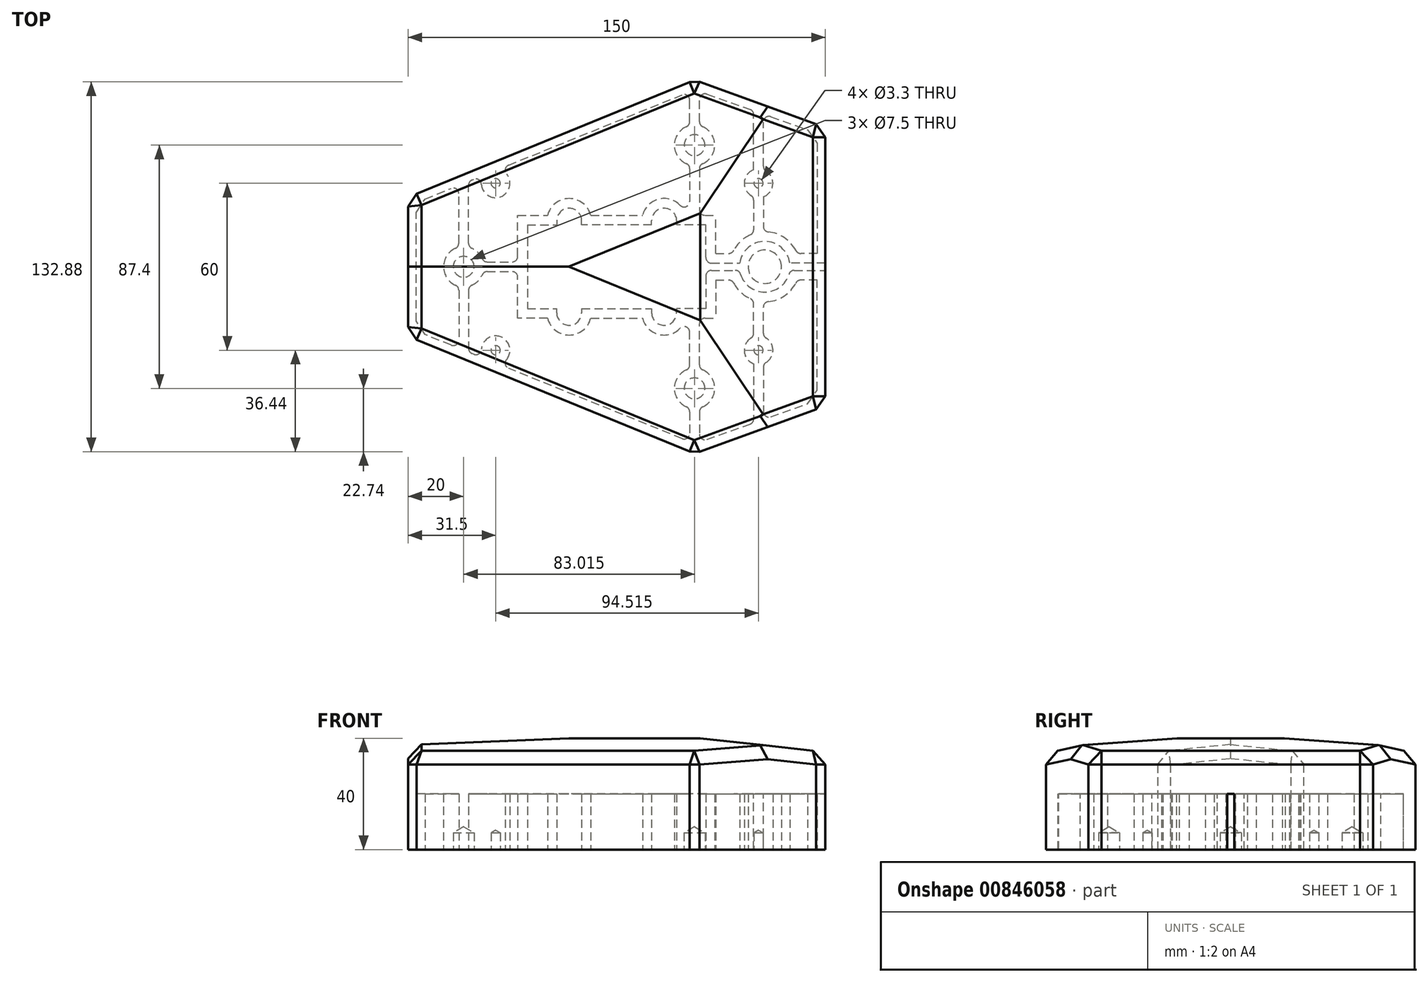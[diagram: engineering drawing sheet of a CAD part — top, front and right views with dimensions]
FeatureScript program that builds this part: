
annotation { "Feature Type Name" : "Feature", "Feature Type Description" : "" }
export const myFeature = defineFeature(function(context is Context, id is Id, definition is map)
    precondition{}
    {
        {
            var Q0;
            Q0=qCreatedBy(makeId("Top.planeOp"),FACE);
            var sketch = newSketch(context, id + "F0", { "sketchPlane" : qUnion([Q0])});
            skLineSegment(sketch, "E0", {"start": v(0, 0) * mm, "end": v(0, -50) * mm});
            skLineSegment(sketch, "E1", {"start": v(0, 0) * mm, "end": v(0, 50) * mm});
            skLineSegment(sketch, "E2", {"start": v(0, 50) * mm, "end": v(-46.98, 67.1) * mm});
            skLineSegment(sketch, "E3", {"start": v(-150, 0) * mm, "end": v(-150, 25) * mm});
            skLineSegment(sketch, "E4", {"start": v(-150, 0) * mm, "end": v(-150, -25) * mm});
            skLineSegment(sketch, "E5", {"start": v(-150, 25) * mm, "end": v(-46.98, 67.1) * mm});
            skLineSegment(sketch, "E6", {"start": v(-150, 0) * mm, "end": v(0, 0) * mm});
            skLineSegment(sketch, "E7.MirrorCS", {"start": v(0, -50) * mm, "end": v(-46.98, -67.1) * mm});
            skLineSegment(sketch, "E8", {"start": v(-150, -25) * mm, "end": v(-46.98, -67.1) * mm});
            skLineSegment(sketch, "E9.bottom", {"start": v(-106.68, 14.6) * mm, "end": v(-96.18, 14.6) * mm});
            skLineSegment(sketch, "E9.top", {"start": v(-106.68, -14.6) * mm, "end": v(-96.18, -14.6) * mm});
            skLineSegment(sketch, "E9.right", {"start": v(-43.33, 14.6) * mm, "end": v(-43.33, -14.6) * mm});
            skLineSegment(sketch, "E10", {"start": v(-96.18, 14.6) * mm, "end": v(-96.18, 16.53) * mm});
            skLineSegment(sketch, "E11", {"start": v(-87.98, 14.6) * mm, "end": v(-87.98, 16.53) * mm});
            skArc(sketch, "E12", {"start": v(-87.98, 16.53) * mm, "mid": v(-92.08, 20.63) * mm, "end": v(-96.18, 16.53) * mm});
            skLineSegment(sketch, "E13.trimOffspring", {"start": v(-87.98, 14.6) * mm, "end": v(-62.02, 14.6) * mm});
            skArc(sketch, "E14.MirrorCS", {"start": v(-62.02, 16.53) * mm, "mid": v(-57.92, 20.63) * mm, "end": v(-53.82, 16.53) * mm});
            skLineSegment(sketch, "E15.MirrorCS", {"start": v(-53.82, 14.6) * mm, "end": v(-53.82, 16.53) * mm});
            skLineSegment(sketch, "E16.MirrorCS", {"start": v(-62.02, 14.6) * mm, "end": v(-62.02, 16.53) * mm});
            skLineSegment(sketch, "E17.MirrorCS", {"start": v(-96.18, -14.6) * mm, "end": v(-96.18, -16.53) * mm});
            skArc(sketch, "E18.MirrorCS", {"start": v(-87.98, -16.53) * mm, "mid": v(-92.08, -20.63) * mm, "end": v(-96.18, -16.53) * mm});
            skLineSegment(sketch, "E19.MirrorCS", {"start": v(-87.98, -14.6) * mm, "end": v(-87.98, -16.53) * mm});
            skLineSegment(sketch, "E20.MirrorCS", {"start": v(-62.03, -14.6) * mm, "end": v(-62.02, -16.53) * mm});
            skArc(sketch, "E21.MirrorCS", {"start": v(-62.02, -16.53) * mm, "mid": v(-57.92, -20.63) * mm, "end": v(-53.83, -16.53) * mm});
            skLineSegment(sketch, "E22.MirrorCS", {"start": v(-53.83, -14.6) * mm, "end": v(-53.83, -16.53) * mm});
            skLineSegment(sketch, "E23.trimOffspring", {"start": v(-87.98, -14.6) * mm, "end": v(-62.03, -14.6) * mm});
            skLineSegment(sketch, "E24.trimOffspring", {"start": v(-53.83, -14.6) * mm, "end": v(-43.33, -14.6) * mm});
            skLineSegment(sketch, "E25.trimOffspring", {"start": v(-53.82, 14.6) * mm, "end": v(-43.33, 14.6) * mm});
            skPoint(sketch, "E26.end.orphan", {"position": v(-43.33, 0) * mm});
            skPoint(sketch, "E26.start.orphan", {"position": v(-106.68, 0) * mm});
            skLineSegment(sketch, "E27.trimOffspring", {"start": v(-106.68, -1.3) * mm, "end": v(-106.68, -14.6) * mm});
            skLineSegment(sketch, "E28", {"start": v(-106.68, 1.3) * mm, "end": v(-106.68, 14.6) * mm});
            skLineSegment(sketch, "E29.MirrorCS", {"start": v(-43.33, 1.3) * mm, "end": v(-35.74, 1.3) * mm});
            skLineSegment(sketch, "E30.MirrorCS", {"start": v(-35.74, 1.3) * mm, "end": v(-35.74, -1.3) * mm});
            skLineSegment(sketch, "E31.MirrorCS", {"start": v(-43.33, -1.3) * mm, "end": v(-35.74, -1.3) * mm});
            skLineSegment(sketch, "E32", {"start": v(-106.68, 1.3) * mm, "end": v(-106.68, -1.3) * mm});
            skSolve(sketch);
        }
        {
            var Q0;
            {var subQ1=sQuery(id+"F0.wireOp",EDGE,"E1");Q0=makeQuery(id+"F0.imprint","IMPRINT",FACE,{"disambiguationData":[TD([[makeQuery(id+"F0.imprint","IMPRINT",EDGE,{"derivedFrom":subQ1}),1.0]])]});}
            var Q1;
            {var subQ1=sQuery(id+"F0.wireOp",EDGE,"E0");Q1=makeQuery(id+"F0.imprint","IMPRINT",FACE,{"disambiguationData":[TD([[makeQuery(id+"F0.imprint","IMPRINT",EDGE,{"derivedFrom":subQ1}),-1.0]])]});}
            var Q2;
            Q2=makeQuery(id+"F0.imprint","IMPRINT",FACE,{"disambiguationData":[TD([[makeQuery(id+"F0.imprint","IMPRINT",EDGE,{"derivedFrom":sQuery(id+"F0.wireOp",EDGE,"E9.bottom")}),-1.0]])]});
            var Q3;
            Q3=makeQuery(id+"F0.imprint","IMPRINT",FACE,{"disambiguationData":[TD([[makeQuery(id+"F0.imprint","IMPRINT",EDGE,{"derivedFrom":sQuery(id+"F0.wireOp",EDGE,"E9.top")}),1.0]])]});
            var Q4;
            {var subQ5=sQuery(id+"F0.wireOp",EDGE,"E29.MirrorCS");Q4=makeQuery(id+"F0.imprint","IMPRINT",FACE,{"disambiguationData":[TD([[makeQuery(id+"F0.imprint","IMPRINT",EDGE,{"derivedFrom":subQ5}),-1.0]])]});}
            var Q5;
            {var subQ5=sQuery(id+"F0.wireOp",EDGE,"E31.MirrorCS");Q5=makeQuery(id+"F0.imprint","IMPRINT",FACE,{"disambiguationData":[TD([[makeQuery(id+"F0.imprint","IMPRINT",EDGE,{"derivedFrom":subQ5}),1.0]])]});}
            extrude(context, id + "F1", {"entities" : qUnion([Q0, Q1, Q2, Q3, Q4, Q5]), "depth" : 30 * mm, "offsetDistance" : 25 * mm});
        }
        {
            var Q0;
            Q0=makeQuery(id+"F1.opExtrude","CAP_FACE",FACE,{"disambiguationData":[OSD([sQuery(id+"F0.wireOp",EDGE,"E0"),sQuery(id+"F0.wireOp",EDGE,"E1"),sQuery(id+"F0.wireOp",EDGE,"E2"),sQuery(id+"F0.wireOp",EDGE,"E3"),sQuery(id+"F0.wireOp",EDGE,"E4"),sQuery(id+"F0.wireOp",EDGE,"E5"),sQuery(id+"F0.wireOp",EDGE,"E7.MirrorCS"),sQuery(id+"F0.wireOp",EDGE,"E8")])],"isStart":true});
            var sketch = newSketch(context, id + "F2", { "sketchPlane" : qUnion([Q0])});
            skLineSegment(sketch, "E33.bottom", {"start": v(-106.68, 14.6) * mm, "end": v(-96.18, 14.6) * mm});
            skLineSegment(sketch, "E33.top", {"start": v(-106.68, -14.6) * mm, "end": v(-96.18, -14.6) * mm});
            skLineSegment(sketch, "E33.right", {"start": v(-43.33, 14.6) * mm, "end": v(-43.33, 1.3) * mm});
            skLineSegment(sketch, "E34", {"start": v(-96.18, 14.6) * mm, "end": v(-96.18, 16.53) * mm});
            skLineSegment(sketch, "E35", {"start": v(-87.98, 14.6) * mm, "end": v(-87.98, 16.53) * mm});
            skArc(sketch, "E36", {"start": v(-87.98, 16.53) * mm, "mid": v(-92.08, 20.63) * mm, "end": v(-96.18, 16.53) * mm});
            skLineSegment(sketch, "E37.trimOffspring", {"start": v(-87.98, 14.6) * mm, "end": v(-62.02, 14.6) * mm});
            skArc(sketch, "E38.MirrorCS", {"start": v(-62.02, 16.53) * mm, "mid": v(-57.92, 20.63) * mm, "end": v(-53.82, 16.53) * mm});
            skLineSegment(sketch, "E39.MirrorCS", {"start": v(-53.82, 14.6) * mm, "end": v(-53.83, 16.53) * mm});
            skLineSegment(sketch, "E40.MirrorCS", {"start": v(-62.02, 14.6) * mm, "end": v(-62.03, 16.53) * mm});
            skLineSegment(sketch, "E41.MirrorCS", {"start": v(-96.18, -14.6) * mm, "end": v(-96.18, -16.53) * mm});
            skArc(sketch, "E42.MirrorCS", {"start": v(-87.98, -16.53) * mm, "mid": v(-92.08, -20.63) * mm, "end": v(-96.18, -16.53) * mm});
            skLineSegment(sketch, "E43.MirrorCS", {"start": v(-87.98, -14.6) * mm, "end": v(-87.98, -16.53) * mm});
            skLineSegment(sketch, "E44.MirrorCS", {"start": v(-62.03, -14.6) * mm, "end": v(-62.02, -16.53) * mm});
            skArc(sketch, "E45.MirrorCS", {"start": v(-62.02, -16.53) * mm, "mid": v(-57.93, -20.63) * mm, "end": v(-53.83, -16.53) * mm});
            skLineSegment(sketch, "E46.MirrorCS", {"start": v(-53.83, -14.6) * mm, "end": v(-53.83, -16.53) * mm});
            skLineSegment(sketch, "E47.trimOffspring", {"start": v(-87.98, -14.6) * mm, "end": v(-62.03, -14.6) * mm});
            skLineSegment(sketch, "E48.trimOffspring", {"start": v(-53.83, -14.6) * mm, "end": v(-43.33, -14.6) * mm});
            skLineSegment(sketch, "E49.trimOffspring", {"start": v(-53.82, 14.6) * mm, "end": v(-43.33, 14.6) * mm});
            skPoint(sketch, "E50.end.orphan", {"position": v(-43.33, 0) * mm});
            skPoint(sketch, "E50.start.orphan", {"position": v(-106.68, 0) * mm});
            skLineSegment(sketch, "E51.trimOffspring", {"start": v(-106.68, -1.3) * mm, "end": v(-106.68, -14.6) * mm});
            skLineSegment(sketch, "E52", {"start": v(-106.68, 1.3) * mm, "end": v(-106.68, 14.6) * mm});
            skLineSegment(sketch, "E53.MirrorCS", {"start": v(-43.33, 1.3) * mm, "end": v(-35.74, 1.3) * mm});
            skLineSegment(sketch, "E54.MirrorCS", {"start": v(-35.73, 1.3) * mm, "end": v(-35.74, -1.3) * mm});
            skLineSegment(sketch, "E55.MirrorCS", {"start": v(-43.33, -1.3) * mm, "end": v(-35.74, -1.3) * mm});
            skLineSegment(sketch, "E56", {"start": v(-106.68, 1.3) * mm, "end": v(-106.68, -1.3) * mm});
            skLineSegment(sketch, "E57", {"start": v(0, 0) * mm, "end": v(-150, 0) * mm});
            skLineSegment(sketch, "E58.trimOffspring", {"start": v(-43.33, -1.3) * mm, "end": v(-43.33, -14.6) * mm});
            skCircle(sketch, "E59", {"center": v(-21.74, 0) * mm, "radius": 6 * mm});
            skCircle(sketch, "E60", {"center": v(-21.74, 0) * mm, "radius": 9.1 * mm});
            skLineSegment(sketch, "E61", {"start": v(-107.08, 0) * mm, "end": v(-107.08, 15) * mm});
            skLineSegment(sketch, "E62", {"start": v(-107.08, 15) * mm, "end": v(-96.58, 15) * mm});
            skLineSegment(sketch, "E63", {"start": v(-96.58, 16.53) * mm, "end": v(-96.58, 15) * mm});
            skLineSegment(sketch, "E64", {"start": v(-75, -14.6) * mm, "end": v(-75, 14.6) * mm});
            skLineSegment(sketch, "E65", {"start": v(-75, 15) * mm, "end": v(-87.58, 15) * mm});
            skLineSegment(sketch, "E66", {"start": v(-87.58, 15) * mm, "end": v(-87.58, 16.53) * mm});
            skLineSegment(sketch, "E67.MirrorCS", {"start": v(-75, 15) * mm, "end": v(-62.43, 15) * mm});
            skLineSegment(sketch, "E68.MirrorCS", {"start": v(-62.43, 15) * mm, "end": v(-62.42, 16.53) * mm});
            skArc(sketch, "E69.MirrorC", {"start": v(-62.42, 16.53) * mm, "mid": v(-57.92, 21.03) * mm, "end": v(-53.42, 16.53) * mm});
            skLineSegment(sketch, "E70.MirrorCS", {"start": v(-42.93, 15) * mm, "end": v(-53.42, 15) * mm});
            skLineSegment(sketch, "E71.MirrorCS", {"start": v(-53.42, 16.53) * mm, "end": v(-53.42, 15) * mm});
            skLineSegment(sketch, "E72.MirrorCS", {"start": v(-42.93, 1.3) * mm, "end": v(-42.93, 15) * mm});
            skLineSegment(sketch, "E73.MirrorCS", {"start": v(-107.08, 0) * mm, "end": v(-107.08, -15) * mm});
            skLineSegment(sketch, "E74.MirrorCS", {"start": v(-107.08, -15) * mm, "end": v(-96.58, -15) * mm});
            skLineSegment(sketch, "E75.MirrorCS", {"start": v(-96.58, -16.53) * mm, "end": v(-96.58, -15) * mm});
            skArc(sketch, "E76.MirrorC", {"start": v(-87.58, -16.53) * mm, "mid": v(-92.08, -21.03) * mm, "end": v(-96.58, -16.53) * mm});
            skLineSegment(sketch, "E77.MirrorCS", {"start": v(-87.58, -15) * mm, "end": v(-87.58, -16.53) * mm});
            skLineSegment(sketch, "E78.MirrorCS", {"start": v(-75, -15) * mm, "end": v(-87.58, -15) * mm});
            skLineSegment(sketch, "E79.MirrorCS", {"start": v(-75, -15) * mm, "end": v(-62.43, -15) * mm});
            skLineSegment(sketch, "E80.MirrorCS", {"start": v(-62.43, -15) * mm, "end": v(-62.42, -16.53) * mm});
            skArc(sketch, "E81.MirrorC", {"start": v(-62.42, -16.53) * mm, "mid": v(-57.92, -21.03) * mm, "end": v(-53.42, -16.53) * mm});
            skLineSegment(sketch, "E82.MirrorCS", {"start": v(-53.42, -16.53) * mm, "end": v(-53.42, -15) * mm});
            skLineSegment(sketch, "E83.MirrorCS", {"start": v(-42.93, -15) * mm, "end": v(-53.42, -15) * mm});
            skLineSegment(sketch, "E84.MirrorCS", {"start": v(-42.93, -1.3) * mm, "end": v(-42.93, -15) * mm});
            skPoint(sketch, "E85.orphan", {"position": v(-42.93, 0) * mm});
            skArc(sketch, "E86.trimOffspring", {"start": v(-87.58, 16.53) * mm, "mid": v(-92.08, 21.03) * mm, "end": v(-96.58, 16.53) * mm});
            skSolve(sketch);
        }
        {
            var Q0;
            Q0=makeQuery(id+"F2.imprint","IMPRINT",FACE,{"disambiguationData":[TD([[makeQuery(id+"F2.imprint","IMPRINT",EDGE,{"derivedFrom":sQuery(id+"F2.wireOp",EDGE,"E33.bottom")}),-1.0]])]});
            var Q1;
            Q1=makeQuery(id+"F2.imprint","IMPRINT",FACE,{"disambiguationData":[TD([[makeQuery(id+"F2.imprint","IMPRINT",EDGE,{"derivedFrom":sQuery(id+"F2.wireOp",EDGE,"E33.top")}),1.0]])]});
            var Q2;
            {var subQ0=sQuery(id+"F2.wireOp",EDGE,"E60");var subQ1=sQuery(id+"F2.wireOp",EDGE,"E57");var subQ2=makeQuery(id+"F2.imprint","INTERSECT",VERTEX,{"disambiguationData":[OD(0.0)],"derivedFrom":[subQ1,subQ0]});Q2=makeQuery(id+"F2.imprint","IMPRINT",FACE,{"disambiguationData":[TD([[makeQuery(id+"F2.imprint","IMPRINT",EDGE,{"disambiguationData":[TD([[subQ2,-1.0]])],"derivedFrom":subQ1}),1.0]])]});}
            var Q3;
            {var subQ0=sQuery(id+"F2.wireOp",EDGE,"E60");var subQ1=sQuery(id+"F2.wireOp",EDGE,"E57");var subQ2=makeQuery(id+"F2.imprint","INTERSECT",VERTEX,{"disambiguationData":[OD(0.0)],"derivedFrom":[subQ1,subQ0]});Q3=makeQuery(id+"F2.imprint","IMPRINT",FACE,{"disambiguationData":[TD([[makeQuery(id+"F2.imprint","IMPRINT",EDGE,{"disambiguationData":[TD([[subQ2,-1.0]])],"derivedFrom":subQ1}),-1.0]])]});}
            var Q4;
            Q4=makeQuery(id+"F2.imprint","IMPRINT",FACE,{"disambiguationData":[TD([[makeQuery(id+"F2.imprint","IMPRINT",EDGE,{"derivedFrom":sQuery(id+"F2.wireOp",EDGE,"E33.bottom")}),1.0]])]});
            var Q5;
            {var subQ7=sQuery(id+"F2.wireOp",EDGE,"E33.right");Q5=makeQuery(id+"F2.imprint","IMPRINT",FACE,{"disambiguationData":[TD([[makeQuery(id+"F2.imprint","IMPRINT",EDGE,{"derivedFrom":subQ7}),-1.0]])]});}
            var Q6;
            {var subQ8=sQuery(id+"F2.wireOp",EDGE,"E44.MirrorCS");Q6=makeQuery(id+"F2.imprint","IMPRINT",FACE,{"disambiguationData":[TD([[makeQuery(id+"F2.imprint","IMPRINT",EDGE,{"derivedFrom":subQ8}),1.0]])]});}
            var Q7;
            Q7=makeQuery(id+"F2.imprint","IMPRINT",FACE,{"disambiguationData":[TD([[makeQuery(id+"F2.imprint","IMPRINT",EDGE,{"derivedFrom":sQuery(id+"F2.wireOp",EDGE,"E33.top")}),-1.0]])]});
            extrude(context, id + "F3", {"entities" : qUnion([Q0, Q1, Q2, Q3, Q4, Q5, Q6, Q7]), "operationType" : NewBodyOperationType.REMOVE, "oppositeDirection" : true, "depth" : 20 * mm, "offsetDistance" : 25 * mm});
        }
        {
            var Q0;
            Q0=makeQuery(id+"F1.opExtrude","CAP_FACE",FACE,{"disambiguationData":[OSD([sQuery(id+"F0.wireOp",EDGE,"E0"),sQuery(id+"F0.wireOp",EDGE,"E1"),sQuery(id+"F0.wireOp",EDGE,"E2"),sQuery(id+"F0.wireOp",EDGE,"E3"),sQuery(id+"F0.wireOp",EDGE,"E4"),sQuery(id+"F0.wireOp",EDGE,"E5"),sQuery(id+"F0.wireOp",EDGE,"E7.MirrorCS"),sQuery(id+"F0.wireOp",EDGE,"E8")])],"isStart":true});
            var sketch = newSketch(context, id + "F4", { "sketchPlane" : qUnion([Q0])});
            skLineSegment(sketch, "E87", {"start": v(-35.74, 1.3) * mm, "end": v(-30.74, 1.3) * mm});
            skLineSegment(sketch, "E88", {"start": v(0, 1.3) * mm, "end": v(0, -1.3) * mm});
            skLineSegment(sketch, "E89", {"start": v(0, -1.3) * mm, "end": v(-12.73, -1.3) * mm});
            skLineSegment(sketch, "E90", {"start": v(-35.74, -1.3) * mm, "end": v(-35.74, 1.3) * mm});
            skCircle(sketch, "E91.0", {"center": v(-21.74, 0) * mm, "radius": 9.1 * mm});
            skLineSegment(sketch, "E92.trimOffspring", {"start": v(-30.74, -1.3) * mm, "end": v(-35.74, -1.3) * mm});
            skLineSegment(sketch, "E93.trimOffspring", {"start": v(-12.73, 1.3) * mm, "end": v(0, 1.3) * mm});
            skSolve(sketch);
        }
        {
            var Q0;
            Q0=makeQuery(id+"F4.imprint","IMPRINT",FACE,{"disambiguationData":[TD([[makeQuery(id+"F4.imprint","IMPRINT",EDGE,{"derivedFrom":sQuery(id+"F4.wireOp",EDGE,"E87")}),-1.0]])]});
            var Q1;
            Q1=makeQuery(id+"F4.imprint","IMPRINT",FACE,{"disambiguationData":[TD([[makeQuery(id+"F4.imprint","IMPRINT",EDGE,{"derivedFrom":sQuery(id+"F4.wireOp",EDGE,"E88")}),-1.0]])]});
            extrude(context, id + "F5", {"entities" : qUnion([Q0, Q1]), "operationType" : NewBodyOperationType.REMOVE, "oppositeDirection" : true, "depth" : 20 * mm, "offsetDistance" : 25 * mm});
        }
        {
            var Q0;
            Q0=makeQuery(id+"F1.opExtrude","CAP_FACE",FACE,{"disambiguationData":[OSD([sQuery(id+"F0.wireOp",EDGE,"E0"),sQuery(id+"F0.wireOp",EDGE,"E1"),sQuery(id+"F0.wireOp",EDGE,"E2"),sQuery(id+"F0.wireOp",EDGE,"E3"),sQuery(id+"F0.wireOp",EDGE,"E4"),sQuery(id+"F0.wireOp",EDGE,"E5"),sQuery(id+"F0.wireOp",EDGE,"E7.MirrorCS"),sQuery(id+"F0.wireOp",EDGE,"E8")])],"isStart":true});
            var sketch = newSketch(context, id + "F6", { "sketchPlane" : qUnion([Q0])});
            skCircle(sketch, "E94", {"center": v(-46.98, -43.7) * mm, "radius": 3.75 * mm});
            skCircle(sketch, "E95.MirrorC", {"center": v(-46.98, 43.7) * mm, "radius": 3.75 * mm});
            skCircle(sketch, "E96", {"center": v(-130, 0) * mm, "radius": 3.75 * mm});
            skLineSegment(sketch, "E97", {"start": v(-23.98, 43.7) * mm, "end": v(-23.98, -43.7) * mm});
            skLineSegment(sketch, "E98", {"start": v(-46.98, 43.7) * mm, "end": v(-23.98, 43.7) * mm});
            skLineSegment(sketch, "E99", {"start": v(-46.98, -43.7) * mm, "end": v(-23.98, -43.7) * mm});
            skCircle(sketch, "E100", {"center": v(-23.98, 30) * mm, "radius": 1.65 * mm});
            skCircle(sketch, "E101", {"center": v(-23.98, -30) * mm, "radius": 1.65 * mm});
            skLineSegment(sketch, "E102", {"start": v(-118.5, 32) * mm, "end": v(-118.5, -30) * mm});
            skLineSegment(sketch, "E103", {"start": v(0, 0) * mm, "end": v(-130, 0) * mm});
            skCircle(sketch, "E104", {"center": v(-118.5, -30) * mm, "radius": 1.65 * mm});
            skCircle(sketch, "E105.MirrorC", {"center": v(-118.5, 30) * mm, "radius": 1.65 * mm});
            skSolve(sketch);
        }
        {
            var Q0;
            Q0=sQuery(id+"F6.wireOp",VERTEX,"E105.MirrorC.center");
            var Q1;
            Q1=sQuery(id+"F6.wireOp",VERTEX,"E102.end");
            var Q2;
            Q2=sQuery(id+"F6.wireOp",VERTEX,"E101.center");
            var Q3;
            Q3=sQuery(id+"F6.wireOp",VERTEX,"E100.center");
            var Q4;
            Q4=sQuery(id+"F6.wireOp",VERTEX,"E103.end");
            var Q5;
            Q5=sQuery(id+"F6.wireOp",VERTEX,"E99.start");
            var Q6;
            Q6=sQuery(id+"F6.wireOp",VERTEX,"E98.start");
            var Q7;
            Q7=makeQuery(id+"F1.opExtrude","SWEPT_BODY",BODY,{"disambiguationData":[OSD([sQuery(id+"F0.wireOp",EDGE,"E0"),sQuery(id+"F0.wireOp",EDGE,"E1"),sQuery(id+"F0.wireOp",EDGE,"E2"),sQuery(id+"F0.wireOp",EDGE,"E3"),sQuery(id+"F0.wireOp",EDGE,"E4"),sQuery(id+"F0.wireOp",EDGE,"E5"),sQuery(id+"F0.wireOp",EDGE,"E7.MirrorCS"),sQuery(id+"F0.wireOp",EDGE,"E8")])]});
            hole(context, id + "F7", {"style" : HoleStyle.SIMPLE, "endStyle" : HoleEndStyle.BLIND, "holeDiameter" : 3.3 * mm, "majorDiameter" : 5 * mm, "holeDepth" : 6 * mm, "isTappedThrough" : true, "tappedDepth" : 12 * mm, "tapClearance" : 3, "locations" : qUnion([Q0, Q1, Q2, Q3, Q4, Q5, Q6]), "scope" : qUnion([Q7])});
        }
        {
            var Q0;
            Q0=makeQuery(id+"F1.opExtrude","CAP_FACE",FACE,{"disambiguationData":[OSD([sQuery(id+"F0.wireOp",EDGE,"E0"),sQuery(id+"F0.wireOp",EDGE,"E1"),sQuery(id+"F0.wireOp",EDGE,"E2"),sQuery(id+"F0.wireOp",EDGE,"E3"),sQuery(id+"F0.wireOp",EDGE,"E4"),sQuery(id+"F0.wireOp",EDGE,"E5"),sQuery(id+"F0.wireOp",EDGE,"E7.MirrorCS"),sQuery(id+"F0.wireOp",EDGE,"E8")])],"isStart":true});
            var sketch = newSketch(context, id + "F8", { "sketchPlane" : qUnion([Q0])});
            skCircle(sketch, "E106", {"center": v(-130, 0) * mm, "radius": 3.75 * mm});
            skCircle(sketch, "E107", {"center": v(-46.98, 43.7) * mm, "radius": 3.75 * mm});
            skCircle(sketch, "E108", {"center": v(-46.98, -43.7) * mm, "radius": 3.75 * mm});
            skSolve(sketch);
        }
        {
            var Q0;
            Q0=sQuery(id+"F8.wireOp",VERTEX,"E106.center");
            var Q1;
            Q1=sQuery(id+"F8.wireOp",VERTEX,"E107.center");
            var Q2;
            Q2=sQuery(id+"F8.wireOp",VERTEX,"E108.center");
            var Q3;
            Q3=makeQuery(id+"F1.opExtrude","SWEPT_BODY",BODY,{"disambiguationData":[OSD([sQuery(id+"F0.wireOp",EDGE,"E0"),sQuery(id+"F0.wireOp",EDGE,"E1"),sQuery(id+"F0.wireOp",EDGE,"E2"),sQuery(id+"F0.wireOp",EDGE,"E3"),sQuery(id+"F0.wireOp",EDGE,"E4"),sQuery(id+"F0.wireOp",EDGE,"E5"),sQuery(id+"F0.wireOp",EDGE,"E7.MirrorCS"),sQuery(id+"F0.wireOp",EDGE,"E8")])]});
            hole(context, id + "F9", {"style" : HoleStyle.SIMPLE, "endStyle" : HoleEndStyle.BLIND, "holeDiameter" : 7.5 * mm, "majorDiameter" : 5 * mm, "holeDepth" : 6 * mm, "isTappedThrough" : true, "tappedDepth" : 12 * mm, "tapClearance" : 3, "locations" : qUnion([Q0, Q1, Q2]), "scope" : qUnion([Q3])});
        }
        {
            var Q0;
            Q0=makeQuery(id+"F1.opExtrude","CAP_FACE",FACE,{"disambiguationData":[OSD([sQuery(id+"F0.wireOp",EDGE,"E0"),sQuery(id+"F0.wireOp",EDGE,"E1"),sQuery(id+"F0.wireOp",EDGE,"E2"),sQuery(id+"F0.wireOp",EDGE,"E3"),sQuery(id+"F0.wireOp",EDGE,"E4"),sQuery(id+"F0.wireOp",EDGE,"E5"),sQuery(id+"F0.wireOp",EDGE,"E7.MirrorCS"),sQuery(id+"F0.wireOp",EDGE,"E8")])],"isStart":false});
            var sketch = newSketch(context, id + "F10", { "sketchPlane" : qUnion([Q0])});
            skLineSegment(sketch, "E109", {"start": v(-23.5, 58.55) * mm, "end": v(-44.8, 0) * mm});
            skLineSegment(sketch, "E110", {"start": v(-44.8, 0) * mm, "end": v(-23.5, -58.55) * mm});
            skLineSegment(sketch, "E111.0.0", {"start": v(-46.98, -67.1) * mm, "end": v(0, -50) * mm});
            skLineSegment(sketch, "E111.0.1", {"start": v(0, -50) * mm, "end": v(0, 50) * mm});
            skLineSegment(sketch, "E111.0.2", {"start": v(0, 50) * mm, "end": v(-46.98, 67.1) * mm});
            skLineSegment(sketch, "E111.0.3", {"start": v(-46.98, 67.1) * mm, "end": v(-150, 25) * mm});
            skLineSegment(sketch, "E111.0.4", {"start": v(-150, 25) * mm, "end": v(-150, -25) * mm});
            skLineSegment(sketch, "E111.0.5", {"start": v(-150, -25) * mm, "end": v(-46.98, -67.1) * mm});
            skLineSegment(sketch, "E112", {"start": v(-150, 0) * mm, "end": v(-44.8, 0) * mm});
            skSolve(sketch);
        }
        {
            var Q0;
            {var subQ4=sQuery(id+"F10.wireOp",EDGE,"E109");Q0=makeQuery(id+"F10.imprint","IMPRINT",FACE,{"disambiguationData":[TD([[makeQuery(id+"F10.imprint","IMPRINT",EDGE,{"derivedFrom":subQ4}),-1.0]])]});}
            var Q1;
            {var subQ3=sQuery(id+"F10.wireOp",EDGE,"E109");Q1=makeQuery(id+"F10.imprint","IMPRINT",FACE,{"disambiguationData":[TD([[makeQuery(id+"F10.imprint","IMPRINT",EDGE,{"derivedFrom":subQ3}),1.0]])]});}
            var Q2;
            {var subQ4=sQuery(id+"F10.wireOp",EDGE,"E110");Q2=makeQuery(id+"F10.imprint","IMPRINT",FACE,{"disambiguationData":[TD([[makeQuery(id+"F10.imprint","IMPRINT",EDGE,{"derivedFrom":subQ4}),-1.0]])]});}
            extrude(context, id + "F11", {"entities" : qUnion([Q0, Q1, Q2]), "operationType" : NewBodyOperationType.ADD, "depth" : 10 * mm, "offsetDistance" : 25 * mm});
        }
        {
            var Q0;
            Q0=makeQuery(id+"F11.opExtrude","CAP_EDGE",EDGE,{"disambiguationData":[OSD([sQuery(id+"F10.wireOp",EDGE,"E111.0.5")])],"isStart":false});
            var Q1;
            Q1=makeQuery(id+"F11.opExtrude","CAP_EDGE",EDGE,{"disambiguationData":[OSD([sQuery(id+"F10.wireOp",EDGE,"E111.0.3")])],"isStart":false});
            var Q2;
            Q2=makeQuery(id+"F11.opExtrude","CAP_EDGE",EDGE,{"disambiguationData":[OSD([sQuery(id+"F10.wireOp",EDGE,"E111.0.1")])],"isStart":false});
            chamfer(context, id + "F12", {"entities" : qUnion([Q0, Q1, Q2]), "chamferType" : ChamferType.TWO_OFFSETS, "width1" : 45 * mm, "oppositeDirection" : false, "width2" : 5 * mm, "tangentPropagation" : true});
        }
        {
            var Q0;
            Q0=makeQuery(id+"F12.opChamfer","BLEND_EDGE",EDGE,{"blendedFrom":[makeQuery(id+"F11.opExtrude","CAP_EDGE",EDGE,{"disambiguationData":[OSD([sQuery(id+"F10.wireOp",EDGE,"E111.0.3")])],"isStart":false}),makeQuery(id+"F11.boolean.opBoolean","MERGE",FACE,{"derivedFrom":[makeQuery(id+"F1.opExtrude","SWEPT_FACE",FACE,{"disambiguationData":[OSD([sQuery(id+"F0.wireOp",EDGE,"E3"),sQuery(id+"F0.wireOp",EDGE,"E4")])]}),makeQuery(id+"F11.opExtrude","SWEPT_FACE",FACE,{"disambiguationData":[OSD([sQuery(id+"F10.wireOp",EDGE,"E111.0.4")])]})]})],"blendedInto":[makeQuery(id+"F11.boolean.opBoolean","MERGE",FACE,{"derivedFrom":[makeQuery(id+"F1.opExtrude","SWEPT_FACE",FACE,{"disambiguationData":[OSD([sQuery(id+"F0.wireOp",EDGE,"E3"),sQuery(id+"F0.wireOp",EDGE,"E4")])]}),makeQuery(id+"F11.opExtrude","SWEPT_FACE",FACE,{"disambiguationData":[OSD([sQuery(id+"F10.wireOp",EDGE,"E111.0.4")])]})]})]});
            var Q1;
            Q1=makeQuery(id+"F12.opChamfer","BLEND_EDGE",EDGE,{"blendedFrom":[makeQuery(id+"F11.opExtrude","CAP_EDGE",EDGE,{"disambiguationData":[OSD([sQuery(id+"F10.wireOp",EDGE,"E111.0.5")])],"isStart":false}),makeQuery(id+"F11.boolean.opBoolean","MERGE",FACE,{"derivedFrom":[makeQuery(id+"F1.opExtrude","SWEPT_FACE",FACE,{"disambiguationData":[OSD([sQuery(id+"F0.wireOp",EDGE,"E3"),sQuery(id+"F0.wireOp",EDGE,"E4")])]}),makeQuery(id+"F11.opExtrude","SWEPT_FACE",FACE,{"disambiguationData":[OSD([sQuery(id+"F10.wireOp",EDGE,"E111.0.4")])]})]})],"blendedInto":[makeQuery(id+"F11.boolean.opBoolean","MERGE",FACE,{"derivedFrom":[makeQuery(id+"F1.opExtrude","SWEPT_FACE",FACE,{"disambiguationData":[OSD([sQuery(id+"F0.wireOp",EDGE,"E3"),sQuery(id+"F0.wireOp",EDGE,"E4")])]}),makeQuery(id+"F11.opExtrude","SWEPT_FACE",FACE,{"disambiguationData":[OSD([sQuery(id+"F10.wireOp",EDGE,"E111.0.4")])]})]})]});
            var Q2;
            {var subQ0=sQuery(id+"F10.wireOp",EDGE,"E111.0.5");Q2=makeQuery(id+"F12.opChamfer","BLEND_EDGE",EDGE,{"blendedFrom":[makeQuery(id+"F11.opExtrude","CAP_EDGE",EDGE,{"disambiguationData":[OSD([subQ0])],"isStart":false}),makeQuery(id+"F11.boolean.opBoolean","MERGE",FACE,{"derivedFrom":[makeQuery(id+"F1.opExtrude","SWEPT_FACE",FACE,{"disambiguationData":[OSD([sQuery(id+"F0.wireOp",EDGE,"E8")])]}),makeQuery(id+"F11.opExtrude","SWEPT_FACE",FACE,{"disambiguationData":[OSD([subQ0])]})]})],"blendedInto":[makeQuery(id+"F11.boolean.opBoolean","MERGE",FACE,{"derivedFrom":[makeQuery(id+"F1.opExtrude","SWEPT_FACE",FACE,{"disambiguationData":[OSD([sQuery(id+"F0.wireOp",EDGE,"E8")])]}),makeQuery(id+"F11.opExtrude","SWEPT_FACE",FACE,{"disambiguationData":[OSD([subQ0])]})]})]});}
            var Q3;
            Q3=makeQuery(id+"F12.opChamfer","BLEND_EDGE",EDGE,{"blendedFrom":[makeQuery(id+"F11.opExtrude","CAP_EDGE",EDGE,{"disambiguationData":[OSD([sQuery(id+"F10.wireOp",EDGE,"E111.0.5")])],"isStart":false}),makeQuery(id+"F11.boolean.opBoolean","MERGE",FACE,{"derivedFrom":[makeQuery(id+"F1.opExtrude","SWEPT_FACE",FACE,{"disambiguationData":[OSD([sQuery(id+"F0.wireOp",EDGE,"E7.MirrorCS")])]}),makeQuery(id+"F11.opExtrude","SWEPT_FACE",FACE,{"disambiguationData":[OSD([sQuery(id+"F10.wireOp",EDGE,"E111.0.0")])]})]})],"blendedInto":[makeQuery(id+"F11.boolean.opBoolean","MERGE",FACE,{"derivedFrom":[makeQuery(id+"F1.opExtrude","SWEPT_FACE",FACE,{"disambiguationData":[OSD([sQuery(id+"F0.wireOp",EDGE,"E7.MirrorCS")])]}),makeQuery(id+"F11.opExtrude","SWEPT_FACE",FACE,{"disambiguationData":[OSD([sQuery(id+"F10.wireOp",EDGE,"E111.0.0")])]})]})]});
            var Q4;
            Q4=makeQuery(id+"F12.opChamfer","BLEND_EDGE",EDGE,{"blendedFrom":[makeQuery(id+"F11.opExtrude","CAP_EDGE",EDGE,{"disambiguationData":[OSD([sQuery(id+"F10.wireOp",EDGE,"E111.0.1")])],"isStart":false}),makeQuery(id+"F11.boolean.opBoolean","MERGE",FACE,{"derivedFrom":[makeQuery(id+"F1.opExtrude","SWEPT_FACE",FACE,{"disambiguationData":[OSD([sQuery(id+"F0.wireOp",EDGE,"E7.MirrorCS")])]}),makeQuery(id+"F11.opExtrude","SWEPT_FACE",FACE,{"disambiguationData":[OSD([sQuery(id+"F10.wireOp",EDGE,"E111.0.0")])]})]})],"blendedInto":[makeQuery(id+"F11.boolean.opBoolean","MERGE",FACE,{"derivedFrom":[makeQuery(id+"F1.opExtrude","SWEPT_FACE",FACE,{"disambiguationData":[OSD([sQuery(id+"F0.wireOp",EDGE,"E7.MirrorCS")])]}),makeQuery(id+"F11.opExtrude","SWEPT_FACE",FACE,{"disambiguationData":[OSD([sQuery(id+"F10.wireOp",EDGE,"E111.0.0")])]})]})]});
            var Q5;
            {var subQ0=sQuery(id+"F10.wireOp",EDGE,"E111.0.1");Q5=makeQuery(id+"F12.opChamfer","BLEND_EDGE",EDGE,{"blendedFrom":[makeQuery(id+"F11.opExtrude","CAP_EDGE",EDGE,{"disambiguationData":[OSD([subQ0])],"isStart":false}),makeQuery(id+"F11.boolean.opBoolean","MERGE",FACE,{"derivedFrom":[makeQuery(id+"F1.opExtrude","SWEPT_FACE",FACE,{"disambiguationData":[OSD([sQuery(id+"F0.wireOp",EDGE,"E0"),sQuery(id+"F0.wireOp",EDGE,"E1")])]}),makeQuery(id+"F11.opExtrude","SWEPT_FACE",FACE,{"disambiguationData":[OSD([subQ0])]})]})],"blendedInto":[makeQuery(id+"F11.boolean.opBoolean","MERGE",FACE,{"derivedFrom":[makeQuery(id+"F1.opExtrude","SWEPT_FACE",FACE,{"disambiguationData":[OSD([sQuery(id+"F0.wireOp",EDGE,"E0"),sQuery(id+"F0.wireOp",EDGE,"E1")])]}),makeQuery(id+"F11.opExtrude","SWEPT_FACE",FACE,{"disambiguationData":[OSD([subQ0])]})]})]});}
            var Q6;
            Q6=makeQuery(id+"F12.opChamfer","BLEND_EDGE",EDGE,{"blendedFrom":[makeQuery(id+"F11.opExtrude","CAP_EDGE",EDGE,{"disambiguationData":[OSD([sQuery(id+"F10.wireOp",EDGE,"E111.0.1")])],"isStart":false}),makeQuery(id+"F11.boolean.opBoolean","MERGE",FACE,{"derivedFrom":[makeQuery(id+"F1.opExtrude","SWEPT_FACE",FACE,{"disambiguationData":[OSD([sQuery(id+"F0.wireOp",EDGE,"E2")])]}),makeQuery(id+"F11.opExtrude","SWEPT_FACE",FACE,{"disambiguationData":[OSD([sQuery(id+"F10.wireOp",EDGE,"E111.0.2")])]})]})],"blendedInto":[makeQuery(id+"F11.boolean.opBoolean","MERGE",FACE,{"derivedFrom":[makeQuery(id+"F1.opExtrude","SWEPT_FACE",FACE,{"disambiguationData":[OSD([sQuery(id+"F0.wireOp",EDGE,"E2")])]}),makeQuery(id+"F11.opExtrude","SWEPT_FACE",FACE,{"disambiguationData":[OSD([sQuery(id+"F10.wireOp",EDGE,"E111.0.2")])]})]})]});
            var Q7;
            Q7=makeQuery(id+"F12.opChamfer","BLEND_EDGE",EDGE,{"blendedFrom":[makeQuery(id+"F11.opExtrude","CAP_EDGE",EDGE,{"disambiguationData":[OSD([sQuery(id+"F10.wireOp",EDGE,"E111.0.3")])],"isStart":false}),makeQuery(id+"F11.boolean.opBoolean","MERGE",FACE,{"derivedFrom":[makeQuery(id+"F1.opExtrude","SWEPT_FACE",FACE,{"disambiguationData":[OSD([sQuery(id+"F0.wireOp",EDGE,"E2")])]}),makeQuery(id+"F11.opExtrude","SWEPT_FACE",FACE,{"disambiguationData":[OSD([sQuery(id+"F10.wireOp",EDGE,"E111.0.2")])]})]})],"blendedInto":[makeQuery(id+"F11.boolean.opBoolean","MERGE",FACE,{"derivedFrom":[makeQuery(id+"F1.opExtrude","SWEPT_FACE",FACE,{"disambiguationData":[OSD([sQuery(id+"F0.wireOp",EDGE,"E2")])]}),makeQuery(id+"F11.opExtrude","SWEPT_FACE",FACE,{"disambiguationData":[OSD([sQuery(id+"F10.wireOp",EDGE,"E111.0.2")])]})]})]});
            var Q8;
            {var subQ0=sQuery(id+"F10.wireOp",EDGE,"E111.0.3");Q8=makeQuery(id+"F12.opChamfer","BLEND_EDGE",EDGE,{"blendedFrom":[makeQuery(id+"F11.opExtrude","CAP_EDGE",EDGE,{"disambiguationData":[OSD([subQ0])],"isStart":false}),makeQuery(id+"F11.boolean.opBoolean","MERGE",FACE,{"derivedFrom":[makeQuery(id+"F1.opExtrude","SWEPT_FACE",FACE,{"disambiguationData":[OSD([sQuery(id+"F0.wireOp",EDGE,"E5")])]}),makeQuery(id+"F11.opExtrude","SWEPT_FACE",FACE,{"disambiguationData":[OSD([subQ0])]})]})],"blendedInto":[makeQuery(id+"F11.boolean.opBoolean","MERGE",FACE,{"derivedFrom":[makeQuery(id+"F1.opExtrude","SWEPT_FACE",FACE,{"disambiguationData":[OSD([sQuery(id+"F0.wireOp",EDGE,"E5")])]}),makeQuery(id+"F11.opExtrude","SWEPT_FACE",FACE,{"disambiguationData":[OSD([subQ0])]})]})]});}
            var Q9;
            Q9=makeQuery(id+"F11.boolean.opBoolean","MERGE",EDGE,{"derivedFrom":[makeQuery(id+"F1.opExtrude","SWEPT_EDGE",EDGE,{"disambiguationData":[OSD([sQuery(id+"F0.wireOp",EDGE,"E1"),sQuery(id+"F0.wireOp",EDGE,"E2")])]}),makeQuery(id+"F11.opExtrude","SWEPT_EDGE",EDGE,{"disambiguationData":[OSD([sQuery(id+"F10.wireOp",EDGE,"E111.0.1"),sQuery(id+"F10.wireOp",EDGE,"E111.0.2")])]})]});
            var Q10;
            Q10=makeQuery(id+"F11.boolean.opBoolean","MERGE",EDGE,{"derivedFrom":[makeQuery(id+"F1.opExtrude","SWEPT_EDGE",EDGE,{"disambiguationData":[OSD([sQuery(id+"F0.wireOp",EDGE,"E2"),sQuery(id+"F0.wireOp",EDGE,"E5")])]}),makeQuery(id+"F11.opExtrude","SWEPT_EDGE",EDGE,{"disambiguationData":[OSD([sQuery(id+"F10.wireOp",EDGE,"E111.0.2"),sQuery(id+"F10.wireOp",EDGE,"E111.0.3")])]})]});
            var Q11;
            Q11=makeQuery(id+"F11.boolean.opBoolean","MERGE",EDGE,{"derivedFrom":[makeQuery(id+"F1.opExtrude","SWEPT_EDGE",EDGE,{"disambiguationData":[OSD([sQuery(id+"F0.wireOp",EDGE,"E0"),sQuery(id+"F0.wireOp",EDGE,"E7.MirrorCS")])]}),makeQuery(id+"F11.opExtrude","SWEPT_EDGE",EDGE,{"disambiguationData":[OSD([sQuery(id+"F10.wireOp",EDGE,"E111.0.0"),sQuery(id+"F10.wireOp",EDGE,"E111.0.1")])]})]});
            var Q12;
            Q12=makeQuery(id+"F11.boolean.opBoolean","MERGE",EDGE,{"derivedFrom":[makeQuery(id+"F1.opExtrude","SWEPT_EDGE",EDGE,{"disambiguationData":[OSD([sQuery(id+"F0.wireOp",EDGE,"E7.MirrorCS"),sQuery(id+"F0.wireOp",EDGE,"E8")])]}),makeQuery(id+"F11.opExtrude","SWEPT_EDGE",EDGE,{"disambiguationData":[OSD([sQuery(id+"F10.wireOp",EDGE,"E111.0.0"),sQuery(id+"F10.wireOp",EDGE,"E111.0.5")])]})]});
            var Q13;
            Q13=makeQuery(id+"F11.boolean.opBoolean","MERGE",EDGE,{"derivedFrom":[makeQuery(id+"F1.opExtrude","SWEPT_EDGE",EDGE,{"disambiguationData":[OSD([sQuery(id+"F0.wireOp",EDGE,"E4"),sQuery(id+"F0.wireOp",EDGE,"E8")])]}),makeQuery(id+"F11.opExtrude","SWEPT_EDGE",EDGE,{"disambiguationData":[OSD([sQuery(id+"F10.wireOp",EDGE,"E111.0.4"),sQuery(id+"F10.wireOp",EDGE,"E111.0.5")])]})]});
            var Q14;
            Q14=makeQuery(id+"F11.boolean.opBoolean","MERGE",EDGE,{"derivedFrom":[makeQuery(id+"F1.opExtrude","SWEPT_EDGE",EDGE,{"disambiguationData":[OSD([sQuery(id+"F0.wireOp",EDGE,"E3"),sQuery(id+"F0.wireOp",EDGE,"E5")])]}),makeQuery(id+"F11.opExtrude","SWEPT_EDGE",EDGE,{"disambiguationData":[OSD([sQuery(id+"F10.wireOp",EDGE,"E111.0.3"),sQuery(id+"F10.wireOp",EDGE,"E111.0.4")])]})]});
            chamfer(context, id + "F13", {"entities" : qUnion([Q0, Q1, Q2, Q3, Q4, Q5, Q6, Q7, Q8, Q9, Q10, Q11, Q12, Q13, Q14]), "width" : 5 * mm, "tangentPropagation" : true});
        }
        {
            var Q0;
            Q0=makeQuery(id+"F5.boolean.opBoolean","COPY",EDGE,{"derivedFrom":makeQuery(id+"F5.opExtrude","SWEPT_EDGE",EDGE,{"disambiguationData":[OSD([sQuery(id+"F4.wireOp",EDGE,"E87"),sQuery(id+"F4.wireOp",EDGE,"E91.0")])]})});
            var Q1;
            Q1=makeQuery(id+"F5.boolean.opBoolean","COPY",EDGE,{"derivedFrom":makeQuery(id+"F5.opExtrude","SWEPT_EDGE",EDGE,{"disambiguationData":[OSD([sQuery(id+"F4.wireOp",EDGE,"E91.0"),sQuery(id+"F4.wireOp",EDGE,"E92.trimOffspring")])]})});
            var Q2;
            Q2=makeQuery(id+"F5.boolean.opBoolean","COPY",EDGE,{"derivedFrom":makeQuery(id+"F5.opExtrude","SWEPT_EDGE",EDGE,{"disambiguationData":[OSD([sQuery(id+"F4.wireOp",EDGE,"E91.0"),sQuery(id+"F4.wireOp",EDGE,"E93.trimOffspring")])]})});
            var Q3;
            Q3=makeQuery(id+"F5.boolean.opBoolean","COPY",EDGE,{"derivedFrom":makeQuery(id+"F5.opExtrude","SWEPT_EDGE",EDGE,{"disambiguationData":[OSD([sQuery(id+"F4.wireOp",EDGE,"E89"),sQuery(id+"F4.wireOp",EDGE,"E91.0")])]})});
            var Q4;
            Q4=makeQuery(id+"F3.boolean.opBoolean","COPY",EDGE,{"derivedFrom":makeQuery(id+"F3.opExtrude","SWEPT_EDGE",EDGE,{"disambiguationData":[OSD([sQuery(id+"F2.wireOp",EDGE,"E33.right"),sQuery(id+"F2.wireOp",EDGE,"E53.MirrorCS")])]})});
            var Q5;
            Q5=makeQuery(id+"F3.boolean.opBoolean","COPY",EDGE,{"derivedFrom":makeQuery(id+"F3.opExtrude","SWEPT_EDGE",EDGE,{"disambiguationData":[OSD([sQuery(id+"F2.wireOp",EDGE,"E55.MirrorCS"),sQuery(id+"F2.wireOp",EDGE,"E58.trimOffspring")])]})});
            fillet(context, id + "F14", {"entities" : qUnion([Q0, Q1, Q2, Q3, Q4, Q5]), "radius" : 2 * mm, "tangentPropagation" : true, "allowEdgeOverflow" : false});
        }
        {
            var Q0;
            {var subQ0=sQuery(id+"F0.wireOp",EDGE,"E1");var subQ1=sQuery(id+"F0.wireOp",EDGE,"E0");var subQ2=sQuery(id+"F0.wireOp",EDGE,"E4");var subQ3=sQuery(id+"F0.wireOp",EDGE,"E3");var subQ4=sQuery(id+"F0.wireOp",EDGE,"E5");var subQ5=sQuery(id+"F0.wireOp",EDGE,"E7.MirrorCS");var subQ6=sQuery(id+"F0.wireOp",EDGE,"E8");var subQ7=sQuery(id+"F0.wireOp",EDGE,"E2");Q0=makeQuery(id+"F3.boolean.opBoolean","SPLIT",FACE,{"disambiguationData":[TD([makeQuery(id+"F1.opExtrude","SWEPT_FACE",FACE,{"disambiguationData":[OSD([subQ7])]})])],"derivedFrom":makeQuery(id+"F1.opExtrude","CAP_FACE",FACE,{"disambiguationData":[OSD([subQ1,subQ0,subQ7,subQ3,subQ2,subQ4,subQ5,subQ6])],"isStart":true})});}
            var sketch = newSketch(context, id + "F15", { "sketchPlane" : qUnion([Q0])});
            skLineSegment(sketch, "E113", {"start": v(-146.76, 26.32) * mm, "end": v(-143.85, 24.37) * mm});
            skLineSegment(sketch, "E114", {"start": v(-150, 21.5) * mm, "end": v(-147.1, 19.55) * mm});
            skArc(sketch, "E115.0.0", {"start": v(-30.42, 2.7) * mm, "mid": v(-21.73, 9.1) * mm, "end": v(-13.05, 2.7) * mm});
            skArc(sketch, "E115.0.1", {"start": v(-13.05, 2.7) * mm, "mid": v(-12.32, 1.69) * mm, "end": v(-11.14, 1.3) * mm});
            skLineSegment(sketch, "E115.0.2", {"start": v(-11.14, 1.3) * mm, "end": v(0, 1.3) * mm});
            skLineSegment(sketch, "E115.0.3", {"start": v(0, 1.3) * mm, "end": v(0, 46.35) * mm});
            skLineSegment(sketch, "E115.0.4", {"start": v(0, 46.35) * mm, "end": v(-3.43, 51.25) * mm});
            skLineSegment(sketch, "E115.0.5", {"start": v(-3.43, 51.25) * mm, "end": v(-45.1, 66.41) * mm});
            skLineSegment(sketch, "E115.0.6", {"start": v(-45.1, 66.41) * mm, "end": v(-48.85, 66.34) * mm});
            skLineSegment(sketch, "E115.0.7", {"start": v(-48.85, 66.34) * mm, "end": v(-146.76, 26.32) * mm});
            skLineSegment(sketch, "E115.0.8", {"start": v(-146.76, 26.32) * mm, "end": v(-150, 21.5) * mm});
            skLineSegment(sketch, "E115.0.9", {"start": v(-150, 21.5) * mm, "end": v(-150, -21.5) * mm});
            skLineSegment(sketch, "E115.0.10", {"start": v(-150, -21.5) * mm, "end": v(-146.76, -26.32) * mm});
            skLineSegment(sketch, "E115.0.11", {"start": v(-146.76, -26.32) * mm, "end": v(-48.85, -66.34) * mm});
            skLineSegment(sketch, "E115.0.12", {"start": v(-48.85, -66.34) * mm, "end": v(-45.1, -66.41) * mm});
            skLineSegment(sketch, "E115.0.13", {"start": v(-45.1, -66.41) * mm, "end": v(-3.43, -51.25) * mm});
            skLineSegment(sketch, "E115.0.14", {"start": v(-3.43, -51.25) * mm, "end": v(0, -46.35) * mm});
            skLineSegment(sketch, "E115.0.15", {"start": v(0, -46.35) * mm, "end": v(0, -1.3) * mm});
            skLineSegment(sketch, "E115.0.16", {"start": v(0, -1.3) * mm, "end": v(-11.14, -1.3) * mm});
            skArc(sketch, "E115.0.17", {"start": v(-11.14, -1.3) * mm, "mid": v(-12.32, -1.69) * mm, "end": v(-13.05, -2.7) * mm});
            skArc(sketch, "E115.0.18", {"start": v(-13.05, -2.7) * mm, "mid": v(-21.74, -9.1) * mm, "end": v(-30.42, -2.7) * mm});
            skArc(sketch, "E115.0.19", {"start": v(-30.42, -2.7) * mm, "mid": v(-31.15, -1.69) * mm, "end": v(-32.33, -1.3) * mm});
            skLineSegment(sketch, "E115.0.20", {"start": v(-32.33, -1.3) * mm, "end": v(-40.93, -1.3) * mm});
            skArc(sketch, "E115.0.43", {"start": v(-42.93, 3.3) * mm, "mid": v(-42.34, 1.89) * mm, "end": v(-40.93, 1.3) * mm});
            skLineSegment(sketch, "E115.0.44", {"start": v(-40.93, 1.3) * mm, "end": v(-32.33, 1.3) * mm});
            skArc(sketch, "E115.0.45", {"start": v(-32.33, 1.3) * mm, "mid": v(-31.15, 1.69) * mm, "end": v(-30.42, 2.7) * mm});
            skCircle(sketch, "E116.0", {"center": v(-130, 0) * mm, "radius": 3.75 * mm});
            skCircle(sketch, "E117.0", {"center": v(-118.5, 30) * mm, "radius": 1.65 * mm});
            skCircle(sketch, "E118.0", {"center": v(-118.5, -30) * mm, "radius": 1.65 * mm});
            skCircle(sketch, "E119.0", {"center": v(-46.98, -43.7) * mm, "radius": 3.75 * mm});
            skCircle(sketch, "E120.0", {"center": v(-23.98, -30) * mm, "radius": 1.65 * mm});
            skPoint(sketch, "E121.0", {"position": v(-23.98, 30) * mm});
            skCircle(sketch, "E122.0", {"center": v(-23.98, 30) * mm, "radius": 1.65 * mm});
            skCircle(sketch, "E123.0", {"center": v(-46.98, 43.7) * mm, "radius": 3.75 * mm});
            skLineSegment(sketch, "E124", {"start": v(-150, -21.5) * mm, "end": v(-147.1, -19.55) * mm});
            skLineSegment(sketch, "E125", {"start": v(-146.76, -26.32) * mm, "end": v(-143.85, -24.37) * mm});
            skLineSegment(sketch, "E126", {"start": v(-48.85, -66.34) * mm, "end": v(-48.85, -62.84) * mm});
            skLineSegment(sketch, "E127", {"start": v(-45.1, -66.41) * mm, "end": v(-45.1, -62.91) * mm});
            skLineSegment(sketch, "E128", {"start": v(-3.43, -51.25) * mm, "end": v(-6.3, -49.24) * mm});
            skLineSegment(sketch, "E129", {"start": v(0, -46.35) * mm, "end": v(-2.87, -44.34) * mm});
            skLineSegment(sketch, "E130", {"start": v(-3.43, 51.25) * mm, "end": v(-6.3, 49.24) * mm});
            skLineSegment(sketch, "E131", {"start": v(0, 46.35) * mm, "end": v(-2.87, 44.34) * mm});
            skLineSegment(sketch, "E132", {"start": v(-48.85, 66.34) * mm, "end": v(-48.78, 62.84) * mm});
            skLineSegment(sketch, "E133", {"start": v(-45.1, 66.41) * mm, "end": v(-45.02, 62.91) * mm});
            skLineSegment(sketch, "E134", {"start": v(-45.02, 62.91) * mm, "end": v(-6.3, 49.24) * mm});
            skLineSegment(sketch, "E135", {"start": v(-6.3, 49.24) * mm, "end": v(-2.87, 44.34) * mm});
            skLineSegment(sketch, "E136", {"start": v(-2.87, 44.34) * mm, "end": v(-2.87, 1.3) * mm});
            skLineSegment(sketch, "E137", {"start": v(-45.02, 62.91) * mm, "end": v(-48.78, 62.84) * mm});
            skLineSegment(sketch, "E138", {"start": v(-48.78, 62.84) * mm, "end": v(-128.25, 30.69) * mm});
            skLineSegment(sketch, "E139", {"start": v(-143.85, 24.37) * mm, "end": v(-147.1, 19.55) * mm});
            skLineSegment(sketch, "E140", {"start": v(-147.1, 19.55) * mm, "end": v(-147.1, -19.55) * mm});
            skLineSegment(sketch, "E141", {"start": v(-147.1, -19.55) * mm, "end": v(-143.85, -24.37) * mm});
            skLineSegment(sketch, "E142", {"start": v(-143.85, -24.37) * mm, "end": v(-131.75, -29.27) * mm});
            skLineSegment(sketch, "E143", {"start": v(-48.85, -62.84) * mm, "end": v(-45.1, -62.91) * mm});
            skLineSegment(sketch, "E144", {"start": v(-45.1, -62.91) * mm, "end": v(-6.3, -49.24) * mm});
            skLineSegment(sketch, "E145", {"start": v(-6.3, -49.24) * mm, "end": v(-2.87, -44.34) * mm});
            skLineSegment(sketch, "E146", {"start": v(-2.87, -44.34) * mm, "end": v(-2.87, -1.3) * mm});
            skCircle(sketch, "E147", {"center": v(-118.5, 30) * mm, "radius": 5.15 * mm});
            skCircle(sketch, "E148", {"center": v(-118.5, -30) * mm, "radius": 5.15 * mm});
            skCircle(sketch, "E149", {"center": v(-23.98, -30) * mm, "radius": 5.15 * mm});
            skCircle(sketch, "E150", {"center": v(-23.98, 30) * mm, "radius": 5.15 * mm});
            skCircle(sketch, "E151", {"center": v(-46.98, 43.7) * mm, "radius": 7.25 * mm});
            skCircle(sketch, "E152", {"center": v(-46.98, -43.7) * mm, "radius": 7.25 * mm});
            skArc(sketch, "E153", {"start": v(-128.25, -7.04) * mm, "mid": v(-122.75, 0) * mm, "end": v(-128.25, 7.04) * mm});
            skArc(sketch, "E154.0.21", {"start": v(-40.93, -1.3) * mm, "mid": v(-42.34, -1.89) * mm, "end": v(-42.93, -3.3) * mm});
            skLineSegment(sketch, "E154.0.42", {"start": v(-42.93, 15) * mm, "end": v(-42.93, 3.3) * mm});
            skLineSegment(sketch, "E155.0.22", {"start": v(-42.93, -3.3) * mm, "end": v(-42.93, -15) * mm});
            skLineSegment(sketch, "E155.0.23", {"start": v(-42.93, -15) * mm, "end": v(-53.42, -15) * mm});
            skLineSegment(sketch, "E155.0.24", {"start": v(-53.42, -15) * mm, "end": v(-53.42, -16.53) * mm});
            skArc(sketch, "E155.0.25", {"start": v(-53.42, -16.53) * mm, "mid": v(-57.92, -21.03) * mm, "end": v(-62.42, -16.53) * mm});
            skLineSegment(sketch, "E155.0.26", {"start": v(-62.42, -16.53) * mm, "end": v(-62.43, -15) * mm});
            skLineSegment(sketch, "E155.0.27", {"start": v(-62.43, -15) * mm, "end": v(-87.58, -15) * mm});
            skLineSegment(sketch, "E155.0.28", {"start": v(-87.58, -15) * mm, "end": v(-87.58, -16.53) * mm});
            skArc(sketch, "E155.0.29", {"start": v(-87.58, -16.53) * mm, "mid": v(-92.08, -21.03) * mm, "end": v(-96.58, -16.53) * mm});
            skLineSegment(sketch, "E155.0.30", {"start": v(-96.58, -16.53) * mm, "end": v(-96.58, -15) * mm});
            skLineSegment(sketch, "E155.0.31", {"start": v(-96.58, -15) * mm, "end": v(-107.08, -15) * mm});
            skLineSegment(sketch, "E155.0.32", {"start": v(-107.08, -15) * mm, "end": v(-107.08, 15) * mm});
            skLineSegment(sketch, "E155.0.33", {"start": v(-107.08, 15) * mm, "end": v(-96.58, 15) * mm});
            skLineSegment(sketch, "E155.0.34", {"start": v(-96.58, 15) * mm, "end": v(-96.58, 16.53) * mm});
            skArc(sketch, "E155.0.35", {"start": v(-96.58, 16.53) * mm, "mid": v(-92.08, 21.03) * mm, "end": v(-87.58, 16.53) * mm});
            skLineSegment(sketch, "E155.0.36", {"start": v(-87.58, 16.53) * mm, "end": v(-87.58, 15) * mm});
            skLineSegment(sketch, "E155.0.37", {"start": v(-87.58, 15) * mm, "end": v(-62.43, 15) * mm});
            skLineSegment(sketch, "E155.0.38", {"start": v(-62.43, 15) * mm, "end": v(-62.42, 16.53) * mm});
            skArc(sketch, "E155.0.39", {"start": v(-62.42, 16.53) * mm, "mid": v(-57.92, 21.03) * mm, "end": v(-53.42, 16.53) * mm});
            skLineSegment(sketch, "E155.0.40", {"start": v(-53.42, 16.53) * mm, "end": v(-53.42, 15) * mm});
            skLineSegment(sketch, "E155.0.41", {"start": v(-53.42, 15) * mm, "end": v(-42.93, 15) * mm});
            skLineSegment(sketch, "E156.bottom", {"start": v(-107.08, 15) * mm, "end": v(-110.58, 15) * mm});
            skLineSegment(sketch, "E156.top", {"start": v(-107.08, 18.5) * mm, "end": v(-110.58, 18.5) * mm});
            skLineSegment(sketch, "E156.left", {"start": v(-107.08, 15) * mm, "end": v(-107.08, 18.5) * mm});
            skLineSegment(sketch, "E156.right", {"start": v(-110.58, 15) * mm, "end": v(-110.58, 18.5) * mm});
            skLineSegment(sketch, "E157.bottom", {"start": v(-107.08, -15) * mm, "end": v(-110.58, -15) * mm});
            skLineSegment(sketch, "E157.top", {"start": v(-107.08, -18.5) * mm, "end": v(-110.58, -18.5) * mm});
            skLineSegment(sketch, "E157.left", {"start": v(-107.08, -15) * mm, "end": v(-107.08, -18.5) * mm});
            skLineSegment(sketch, "E157.right", {"start": v(-110.58, -15) * mm, "end": v(-110.58, -18.5) * mm});
            skLineSegment(sketch, "E158", {"start": v(-75, 15) * mm, "end": v(-75, -15) * mm});
            skLineSegment(sketch, "E159", {"start": v(-107.08, 0) * mm, "end": v(-75, 0) * mm});
            skLineSegment(sketch, "E160.MirrorCS", {"start": v(-39.43, 15) * mm, "end": v(-39.43, 18.5) * mm});
            skLineSegment(sketch, "E161.MirrorCS", {"start": v(-42.93, 18.5) * mm, "end": v(-39.43, 18.5) * mm});
            skLineSegment(sketch, "E162.MirrorCS", {"start": v(-39.43, -15) * mm, "end": v(-39.42, -18.5) * mm});
            skLineSegment(sketch, "E163.MirrorCS", {"start": v(-42.92, -18.5) * mm, "end": v(-39.42, -18.5) * mm});
            skLineSegment(sketch, "E164", {"start": v(-42.93, -4.8) * mm, "end": v(-39.43, -4.8) * mm});
            skLineSegment(sketch, "E165", {"start": v(-39.43, -4.8) * mm, "end": v(-39.43, -1.3) * mm});
            skLineSegment(sketch, "E166.MirrorCS", {"start": v(-42.93, 4.8) * mm, "end": v(-39.43, 4.8) * mm});
            skLineSegment(sketch, "E167.MirrorCS", {"start": v(-39.43, 4.8) * mm, "end": v(-39.43, 1.3) * mm});
            skCircle(sketch, "E168", {"center": v(-21.74, 0) * mm, "radius": 12.6 * mm});
            skLineSegment(sketch, "E169", {"start": v(-39.43, 4.8) * mm, "end": v(-33.38, 4.8) * mm});
            skLineSegment(sketch, "E170", {"start": v(-39.43, -4.8) * mm, "end": v(-33.38, -4.8) * mm});
            skLineSegment(sketch, "E171", {"start": v(-39.43, -4.8) * mm, "end": v(-39.42, -15) * mm});
            skLineSegment(sketch, "E172", {"start": v(-39.43, 4.8) * mm, "end": v(-39.43, 15) * mm});
            skLineSegment(sketch, "E173", {"start": v(-2.87, -1.3) * mm, "end": v(-2.87, -4.8) * mm});
            skLineSegment(sketch, "E174", {"start": v(-2.87, -4.8) * mm, "end": v(-10.09, -4.8) * mm});
            skLineSegment(sketch, "E175", {"start": v(-2.87, 1.3) * mm, "end": v(-2.87, 4.8) * mm});
            skLineSegment(sketch, "E176", {"start": v(-2.87, 4.8) * mm, "end": v(-10.09, 4.8) * mm});
            skCircle(sketch, "E177", {"center": v(-57.92, -16.53) * mm, "radius": 8 * mm});
            skCircle(sketch, "E178.MirrorC", {"center": v(-92.07, -16.53) * mm, "radius": 8 * mm});
            skLineSegment(sketch, "E179", {"start": v(-107.08, -18.5) * mm, "end": v(-42.92, -18.5) * mm});
            skLineSegment(sketch, "E180", {"start": v(-110.58, 15) * mm, "end": v(-110.58, -15) * mm});
            skLineSegment(sketch, "E181.MirrorCS", {"start": v(-107.08, 18.5) * mm, "end": v(-42.92, 18.5) * mm});
            skCircle(sketch, "E182.MirrorC", {"center": v(-92.07, 16.53) * mm, "radius": 8 * mm});
            skCircle(sketch, "E183.MirrorC", {"center": v(-57.93, 16.53) * mm, "radius": 8 * mm});
            skLineSegment(sketch, "E184", {"start": v(-131.75, 7.04) * mm, "end": v(-131.75, 29.27) * mm});
            skLineSegment(sketch, "E185.trimOffspring", {"start": v(-128.25, 7.04) * mm, "end": v(-128.25, 30.69) * mm});
            skPoint(sketch, "E186.orphan", {"position": v(-128.25, 0) * mm});
            skArc(sketch, "E187.trimOffspring", {"start": v(-131.75, 7.04) * mm, "mid": v(-137.25, 0) * mm, "end": v(-131.75, -7.04) * mm});
            skLineSegment(sketch, "E188.trimOffspring", {"start": v(-131.75, 29.27) * mm, "end": v(-143.85, 24.37) * mm});
            skLineSegment(sketch, "E189", {"start": v(-131.75, -7.04) * mm, "end": v(-131.75, -29.27) * mm});
            skLineSegment(sketch, "E190", {"start": v(-128.25, -7.04) * mm, "end": v(-128.25, -30.7) * mm});
            skLineSegment(sketch, "E191.trimOffspring", {"start": v(-128.25, -30.7) * mm, "end": v(-48.85, -62.84) * mm});
            skLineSegment(sketch, "E192", {"start": v(-46.98, 43.7) * mm, "end": v(-46.98, 62.87) * mm});
            skLineSegment(sketch, "E193", {"start": v(-46.98, 43.7) * mm, "end": v(-48.73, 43.7) * mm});
            skLineSegment(sketch, "E194", {"start": v(-48.73, 43.7) * mm, "end": v(-45.23, 43.7) * mm});
            skLineSegment(sketch, "E195", {"start": v(-45.23, 43.7) * mm, "end": v(-45.23, 62.9) * mm});
            skLineSegment(sketch, "E196", {"start": v(-48.73, 43.7) * mm, "end": v(-48.73, 62.84) * mm});
            skLineSegment(sketch, "E197", {"start": v(-48.73, 43.7) * mm, "end": v(-48.73, 18.5) * mm});
            skLineSegment(sketch, "E198", {"start": v(-45.23, 43.7) * mm, "end": v(-45.23, 18.5) * mm});
            skLineSegment(sketch, "E199", {"start": v(-46.98, -43.7) * mm, "end": v(-45.23, -43.7) * mm});
            skLineSegment(sketch, "E200", {"start": v(-45.23, -43.7) * mm, "end": v(-48.73, -43.7) * mm});
            skLineSegment(sketch, "E201", {"start": v(-48.73, -43.7) * mm, "end": v(-48.73, -18.5) * mm});
            skLineSegment(sketch, "E202", {"start": v(-45.23, -43.7) * mm, "end": v(-45.23, -18.5) * mm});
            skLineSegment(sketch, "E203", {"start": v(-48.73, -43.7) * mm, "end": v(-48.73, -62.84) * mm});
            skLineSegment(sketch, "E204", {"start": v(-45.23, -43.7) * mm, "end": v(-45.23, -62.9) * mm});
            skLineSegment(sketch, "E205", {"start": v(-130, 0) * mm, "end": v(-130, 1.75) * mm});
            skLineSegment(sketch, "E206", {"start": v(-130, 1.75) * mm, "end": v(-130, -1.75) * mm});
            skLineSegment(sketch, "E207", {"start": v(-130, -1.75) * mm, "end": v(-110.58, -1.75) * mm});
            skLineSegment(sketch, "E208", {"start": v(-130, 1.75) * mm, "end": v(-110.58, 1.75) * mm});
            skLineSegment(sketch, "E209", {"start": v(-23.98, 30) * mm, "end": v(-25.73, 30) * mm});
            skLineSegment(sketch, "E210", {"start": v(-25.73, 30) * mm, "end": v(-22.23, 30) * mm});
            skLineSegment(sketch, "E211", {"start": v(-22.23, 30) * mm, "end": v(-22.23, 54.87) * mm});
            skLineSegment(sketch, "E212", {"start": v(-25.73, 30) * mm, "end": v(-25.73, 56.1) * mm});
            skLineSegment(sketch, "E213", {"start": v(-25.73, 56.1) * mm, "end": v(-25.73, 11.95) * mm});
            skLineSegment(sketch, "E214", {"start": v(-22.23, 30) * mm, "end": v(-22.23, 12.6) * mm});
            skLineSegment(sketch, "E215", {"start": v(-23.98, -30) * mm, "end": v(-25.73, -30) * mm});
            skLineSegment(sketch, "E216", {"start": v(-25.73, -30) * mm, "end": v(-22.23, -30) * mm});
            skLineSegment(sketch, "E217", {"start": v(-22.23, -30) * mm, "end": v(-22.23, -12.6) * mm});
            skLineSegment(sketch, "E218", {"start": v(-22.23, -12.6) * mm, "end": v(-22.23, -54.86) * mm});
            skLineSegment(sketch, "E219", {"start": v(-25.73, -30) * mm, "end": v(-25.73, -56.1) * mm});
            skLineSegment(sketch, "E220", {"start": v(-25.73, -56.1) * mm, "end": v(-25.73, -11.95) * mm});
            skSolve(sketch);
        }
        {
            var Q0;
            Q0=makeQuery(id+"F15.imprint","IMPRINT",FACE,{"disambiguationData":[TD([[makeQuery(id+"F15.imprint","IMPRINT",EDGE,{"derivedFrom":sQuery(id+"F15.wireOp",EDGE,"E139")}),1.0]])]});
            var Q1;
            {var subQ11=sQuery(id+"F15.wireOp",EDGE,"E157.top");Q1=makeQuery(id+"F15.imprint","IMPRINT",FACE,{"disambiguationData":[TD([[makeQuery(id+"F15.imprint","IMPRINT",EDGE,{"derivedFrom":subQ11}),1.0]])]});}
            var Q2;
            {var subQ18=sQuery(id+"F15.wireOp",EDGE,"E156.top");Q2=makeQuery(id+"F15.imprint","IMPRINT",FACE,{"disambiguationData":[TD([[makeQuery(id+"F15.imprint","IMPRINT",EDGE,{"derivedFrom":subQ18}),-1.0]])]});}
            var Q3;
            {var subQ5=sQuery(id+"F15.wireOp",EDGE,"E135");Q3=makeQuery(id+"F15.imprint","IMPRINT",FACE,{"disambiguationData":[TD([[makeQuery(id+"F15.imprint","IMPRINT",EDGE,{"derivedFrom":subQ5}),-1.0]])]});}
            var Q4;
            Q4=makeQuery(id+"F15.imprint","IMPRINT",FACE,{"disambiguationData":[TD([[makeQuery(id+"F15.imprint","IMPRINT",EDGE,{"derivedFrom":sQuery(id+"F15.wireOp",EDGE,"E160.MirrorCS")}),-1.0]])]});
            var Q5;
            Q5=makeQuery(id+"F15.imprint","IMPRINT",FACE,{"disambiguationData":[TD([[makeQuery(id+"F15.imprint","IMPRINT",EDGE,{"derivedFrom":sQuery(id+"F15.wireOp",EDGE,"E162.MirrorCS")}),1.0]])]});
            var Q6;
            {var subQ0=sQuery(id+"F15.wireOp",EDGE,"E145");Q6=makeQuery(id+"F15.imprint","IMPRINT",FACE,{"disambiguationData":[TD([[makeQuery(id+"F15.imprint","IMPRINT",EDGE,{"derivedFrom":subQ0}),1.0]])]});}
            extrude(context, id + "F16", {"entities" : qUnion([Q0, Q1, Q2, Q3, Q4, Q5, Q6]), "operationType" : NewBodyOperationType.REMOVE, "oppositeDirection" : true, "depth" : 20 * mm, "offsetDistance" : 25 * mm});
        }
        {
            var Q0;
            {var subQ0=sQuery(id+"F15.wireOp",EDGE,"E147");var subQ1=sQuery(id+"F15.wireOp",EDGE,"E138");Q0=makeQuery(id+"F16.boolean.opBoolean","COPY",EDGE,{"derivedFrom":makeQuery(id+"F16.opExtrude","SWEPT_EDGE",EDGE,{"disambiguationData":[OSD([subQ1,subQ0]),TDD([makeQuery(id+"F15.imprint","INTERSECT",VERTEX,{"disambiguationData":[OD(0.0)],"derivedFrom":[subQ1,subQ0]})])]})});}
            var Q1;
            {var subQ0=sQuery(id+"F15.wireOp",EDGE,"E148");var subQ1=sQuery(id+"F15.wireOp",EDGE,"E142");Q1=makeQuery(id+"F16.boolean.opBoolean","COPY",EDGE,{"derivedFrom":makeQuery(id+"F16.opExtrude","SWEPT_EDGE",EDGE,{"disambiguationData":[OSD([subQ1,subQ0]),TDD([makeQuery(id+"F15.imprint","INTERSECT",VERTEX,{"disambiguationData":[OD(1.0)],"derivedFrom":[subQ1,subQ0]})])]})});}
            var Q2;
            {var subQ0=sQuery(id+"F15.wireOp",EDGE,"E148");var subQ1=sQuery(id+"F15.wireOp",EDGE,"E142");Q2=makeQuery(id+"F16.boolean.opBoolean","COPY",EDGE,{"derivedFrom":makeQuery(id+"F16.opExtrude","SWEPT_EDGE",EDGE,{"disambiguationData":[OSD([subQ1,subQ0]),TDD([makeQuery(id+"F15.imprint","INTERSECT",VERTEX,{"disambiguationData":[OD(0.0)],"derivedFrom":[subQ1,subQ0]})])]})});}
            var Q3;
            Q3=makeQuery(id+"F16.boolean.opBoolean","COPY",EDGE,{"derivedFrom":makeQuery(id+"F16.opExtrude","SWEPT_EDGE",EDGE,{"disambiguationData":[OSD([sQuery(id+"F15.wireOp",EDGE,"E168"),sQuery(id+"F15.wireOp",EDGE,"E170")])]})});
            var Q4;
            Q4=makeQuery(id+"F16.boolean.opBoolean","COPY",EDGE,{"derivedFrom":makeQuery(id+"F16.opExtrude","SWEPT_EDGE",EDGE,{"disambiguationData":[OSD([sQuery(id+"F15.wireOp",EDGE,"E168"),sQuery(id+"F15.wireOp",EDGE,"E174")])]})});
            var Q5;
            Q5=makeQuery(id+"F16.boolean.opBoolean","COPY",EDGE,{"derivedFrom":makeQuery(id+"F16.opExtrude","SWEPT_EDGE",EDGE,{"disambiguationData":[OSD([sQuery(id+"F15.wireOp",EDGE,"E168"),sQuery(id+"F15.wireOp",EDGE,"E176")])]})});
            var Q6;
            Q6=makeQuery(id+"F16.boolean.opBoolean","COPY",EDGE,{"derivedFrom":makeQuery(id+"F16.opExtrude","SWEPT_EDGE",EDGE,{"disambiguationData":[OSD([sQuery(id+"F15.wireOp",EDGE,"E168"),sQuery(id+"F15.wireOp",EDGE,"E169")])]})});
            var Q7;
            Q7=makeQuery(id+"F16.boolean.opBoolean","COPY",EDGE,{"derivedFrom":makeQuery(id+"F16.opExtrude","SWEPT_EDGE",EDGE,{"disambiguationData":[OSD([sQuery(id+"F15.wireOp",EDGE,"E138"),sQuery(id+"F15.wireOp",EDGE,"E185.trimOffspring")])]})});
            var Q8;
            Q8=makeQuery(id+"F16.boolean.opBoolean","COPY",EDGE,{"derivedFrom":makeQuery(id+"F16.opExtrude","SWEPT_EDGE",EDGE,{"disambiguationData":[OSD([sQuery(id+"F15.wireOp",EDGE,"E184"),sQuery(id+"F15.wireOp",EDGE,"E188.trimOffspring")])]})});
            var Q9;
            Q9=makeQuery(id+"F16.boolean.opBoolean","COPY",EDGE,{"derivedFrom":makeQuery(id+"F16.opExtrude","SWEPT_EDGE",EDGE,{"disambiguationData":[OSD([sQuery(id+"F15.wireOp",EDGE,"E184"),sQuery(id+"F15.wireOp",EDGE,"E187.trimOffspring")])]})});
            var Q10;
            Q10=makeQuery(id+"F16.boolean.opBoolean","COPY",EDGE,{"derivedFrom":makeQuery(id+"F16.opExtrude","SWEPT_EDGE",EDGE,{"disambiguationData":[OSD([sQuery(id+"F15.wireOp",EDGE,"E153"),sQuery(id+"F15.wireOp",EDGE,"E185.trimOffspring")])]})});
            var Q11;
            Q11=makeQuery(id+"F16.boolean.opBoolean","COPY",EDGE,{"derivedFrom":makeQuery(id+"F16.opExtrude","SWEPT_EDGE",EDGE,{"disambiguationData":[OSD([sQuery(id+"F15.wireOp",EDGE,"E153"),sQuery(id+"F15.wireOp",EDGE,"E190")])]})});
            var Q12;
            Q12=makeQuery(id+"F16.boolean.opBoolean","COPY",EDGE,{"derivedFrom":makeQuery(id+"F16.opExtrude","SWEPT_EDGE",EDGE,{"disambiguationData":[OSD([sQuery(id+"F15.wireOp",EDGE,"E187.trimOffspring"),sQuery(id+"F15.wireOp",EDGE,"E189")])]})});
            var Q13;
            Q13=makeQuery(id+"F16.boolean.opBoolean","COPY",EDGE,{"derivedFrom":makeQuery(id+"F16.opExtrude","SWEPT_EDGE",EDGE,{"disambiguationData":[OSD([sQuery(id+"F15.wireOp",EDGE,"E142"),sQuery(id+"F15.wireOp",EDGE,"E189")])]})});
            var Q14;
            Q14=makeQuery(id+"F16.boolean.opBoolean","COPY",EDGE,{"derivedFrom":makeQuery(id+"F16.opExtrude","SWEPT_EDGE",EDGE,{"disambiguationData":[OSD([sQuery(id+"F15.wireOp",EDGE,"E190"),sQuery(id+"F15.wireOp",EDGE,"E191.trimOffspring")])]})});
            var Q15;
            Q15=makeQuery(id+"F16.boolean.opBoolean","COPY",EDGE,{"derivedFrom":makeQuery(id+"F16.opExtrude","SWEPT_EDGE",EDGE,{"disambiguationData":[OSD([sQuery(id+"F15.wireOp",EDGE,"E179"),sQuery(id+"F15.wireOp",EDGE,"E201")])]})});
            var Q16;
            Q16=makeQuery(id+"F16.boolean.opBoolean","COPY",EDGE,{"derivedFrom":makeQuery(id+"F16.opExtrude","SWEPT_EDGE",EDGE,{"disambiguationData":[OSD([sQuery(id+"F15.wireOp",EDGE,"E179"),sQuery(id+"F15.wireOp",EDGE,"E202")])]})});
            var Q17;
            Q17=makeQuery(id+"F16.boolean.opBoolean","COPY",EDGE,{"derivedFrom":makeQuery(id+"F16.opExtrude","SWEPT_EDGE",EDGE,{"disambiguationData":[OSD([sQuery(id+"F15.wireOp",EDGE,"E152"),sQuery(id+"F15.wireOp",EDGE,"E201")])]})});
            var Q18;
            Q18=makeQuery(id+"F16.boolean.opBoolean","COPY",EDGE,{"derivedFrom":makeQuery(id+"F16.opExtrude","SWEPT_EDGE",EDGE,{"disambiguationData":[OSD([sQuery(id+"F15.wireOp",EDGE,"E126"),sQuery(id+"F15.wireOp",EDGE,"E143"),sQuery(id+"F15.wireOp",EDGE,"E191.trimOffspring")])]})});
            var Q19;
            Q19=makeQuery(id+"F16.boolean.opBoolean","COPY",EDGE,{"derivedFrom":makeQuery(id+"F16.opExtrude","SWEPT_EDGE",EDGE,{"disambiguationData":[OSD([sQuery(id+"F15.wireOp",EDGE,"E127"),sQuery(id+"F15.wireOp",EDGE,"E143"),sQuery(id+"F15.wireOp",EDGE,"E144")])]})});
            var Q20;
            Q20=makeQuery(id+"F16.boolean.opBoolean","COPY",EDGE,{"derivedFrom":makeQuery(id+"F16.opExtrude","SWEPT_EDGE",EDGE,{"disambiguationData":[OSD([sQuery(id+"F15.wireOp",EDGE,"E152"),sQuery(id+"F15.wireOp",EDGE,"E204")])]})});
            var Q21;
            Q21=makeQuery(id+"F16.boolean.opBoolean","COPY",EDGE,{"derivedFrom":makeQuery(id+"F16.opExtrude","SWEPT_EDGE",EDGE,{"disambiguationData":[OSD([sQuery(id+"F15.wireOp",EDGE,"E152"),sQuery(id+"F15.wireOp",EDGE,"E203")])]})});
            var Q22;
            Q22=makeQuery(id+"F16.boolean.opBoolean","COPY",EDGE,{"derivedFrom":makeQuery(id+"F16.opExtrude","SWEPT_EDGE",EDGE,{"disambiguationData":[OSD([sQuery(id+"F15.wireOp",EDGE,"E152"),sQuery(id+"F15.wireOp",EDGE,"E202")])]})});
            var Q23;
            {var subQ0=sQuery(id+"F15.wireOp",EDGE,"E147");var subQ1=sQuery(id+"F15.wireOp",EDGE,"E138");Q23=makeQuery(id+"F16.boolean.opBoolean","COPY",EDGE,{"derivedFrom":makeQuery(id+"F16.opExtrude","SWEPT_EDGE",EDGE,{"disambiguationData":[OSD([subQ1,subQ0]),TDD([makeQuery(id+"F15.imprint","INTERSECT",VERTEX,{"disambiguationData":[OD(1.0)],"derivedFrom":[subQ1,subQ0]})])]})});}
            var Q24;
            Q24=makeQuery(id+"F16.boolean.opBoolean","COPY",EDGE,{"derivedFrom":makeQuery(id+"F16.opExtrude","SWEPT_EDGE",EDGE,{"disambiguationData":[OSD([sQuery(id+"F15.wireOp",EDGE,"E151"),sQuery(id+"F15.wireOp",EDGE,"E197")])]})});
            var Q25;
            Q25=makeQuery(id+"F16.boolean.opBoolean","COPY",EDGE,{"derivedFrom":makeQuery(id+"F16.opExtrude","SWEPT_EDGE",EDGE,{"disambiguationData":[OSD([sQuery(id+"F15.wireOp",EDGE,"E151"),sQuery(id+"F15.wireOp",EDGE,"E198")])]})});
            var Q26;
            Q26=makeQuery(id+"F16.boolean.opBoolean","COPY",EDGE,{"derivedFrom":makeQuery(id+"F16.opExtrude","SWEPT_EDGE",EDGE,{"disambiguationData":[OSD([sQuery(id+"F15.wireOp",EDGE,"E181.MirrorCS"),sQuery(id+"F15.wireOp",EDGE,"E197")])]})});
            var Q27;
            Q27=makeQuery(id+"F16.boolean.opBoolean","COPY",EDGE,{"derivedFrom":makeQuery(id+"F16.opExtrude","SWEPT_EDGE",EDGE,{"disambiguationData":[OSD([sQuery(id+"F15.wireOp",EDGE,"E181.MirrorCS"),sQuery(id+"F15.wireOp",EDGE,"E198")])]})});
            var Q28;
            Q28=makeQuery(id+"F16.boolean.opBoolean","COPY",EDGE,{"derivedFrom":makeQuery(id+"F16.opExtrude","SWEPT_EDGE",EDGE,{"disambiguationData":[OSD([sQuery(id+"F15.wireOp",EDGE,"E132"),sQuery(id+"F15.wireOp",EDGE,"E137"),sQuery(id+"F15.wireOp",EDGE,"E138")])]})});
            var Q29;
            Q29=makeQuery(id+"F16.boolean.opBoolean","COPY",EDGE,{"derivedFrom":makeQuery(id+"F16.opExtrude","SWEPT_EDGE",EDGE,{"disambiguationData":[OSD([sQuery(id+"F15.wireOp",EDGE,"E133"),sQuery(id+"F15.wireOp",EDGE,"E134"),sQuery(id+"F15.wireOp",EDGE,"E137")])]})});
            var Q30;
            Q30=makeQuery(id+"F16.boolean.opBoolean","COPY",EDGE,{"derivedFrom":makeQuery(id+"F16.opExtrude","SWEPT_EDGE",EDGE,{"disambiguationData":[OSD([sQuery(id+"F15.wireOp",EDGE,"E151"),sQuery(id+"F15.wireOp",EDGE,"E195")])]})});
            var Q31;
            Q31=makeQuery(id+"F16.boolean.opBoolean","COPY",EDGE,{"derivedFrom":makeQuery(id+"F16.opExtrude","SWEPT_EDGE",EDGE,{"disambiguationData":[OSD([sQuery(id+"F15.wireOp",EDGE,"E151"),sQuery(id+"F15.wireOp",EDGE,"E196")])]})});
            fillet(context, id + "F17", {"entities" : qUnion([Q0, Q1, Q2, Q3, Q4, Q5, Q6, Q7, Q8, Q9, Q10, Q11, Q12, Q13, Q14, Q15, Q16, Q17, Q18, Q19, Q20, Q21, Q22, Q23, Q24, Q25, Q26, Q27, Q28, Q29, Q30, Q31]), "radius" : 2 * mm, "tangentPropagation" : true, "allowEdgeOverflow" : false});
        }
        {
            var Q0;
            Q0=makeQuery(id+"F17.opFillet","BLEND_EDGE",EDGE,{"blendedFrom":[makeQuery(id+"F16.boolean.opBoolean","COPY",EDGE,{"derivedFrom":makeQuery(id+"F16.opExtrude","SWEPT_EDGE",EDGE,{"disambiguationData":[OSD([sQuery(id+"F15.wireOp",EDGE,"E133"),sQuery(id+"F15.wireOp",EDGE,"E134"),sQuery(id+"F15.wireOp",EDGE,"E137")])]})}),makeQuery(id+"F16.boolean.opBoolean","COPY",FACE,{"derivedFrom":makeQuery(id+"F16.opExtrude","SWEPT_FACE",FACE,{"disambiguationData":[OSD([sQuery(id+"F15.wireOp",EDGE,"E195")])]})})],"blendedInto":[makeQuery(id+"F16.boolean.opBoolean","COPY",FACE,{"derivedFrom":makeQuery(id+"F16.opExtrude","SWEPT_FACE",FACE,{"disambiguationData":[OSD([sQuery(id+"F15.wireOp",EDGE,"E195")])]})})]});
            var Q1;
            Q1=makeQuery(id+"F17.opFillet","BLEND_EDGE",EDGE,{"blendedFrom":[makeQuery(id+"F16.boolean.opBoolean","COPY",EDGE,{"derivedFrom":makeQuery(id+"F16.opExtrude","SWEPT_EDGE",EDGE,{"disambiguationData":[OSD([sQuery(id+"F15.wireOp",EDGE,"E126"),sQuery(id+"F15.wireOp",EDGE,"E143"),sQuery(id+"F15.wireOp",EDGE,"E191.trimOffspring")])]})}),makeQuery(id+"F16.boolean.opBoolean","COPY",FACE,{"derivedFrom":makeQuery(id+"F16.opExtrude","SWEPT_FACE",FACE,{"disambiguationData":[OSD([sQuery(id+"F15.wireOp",EDGE,"E203")])]})})],"blendedInto":[makeQuery(id+"F16.boolean.opBoolean","COPY",FACE,{"derivedFrom":makeQuery(id+"F16.opExtrude","SWEPT_FACE",FACE,{"disambiguationData":[OSD([sQuery(id+"F15.wireOp",EDGE,"E203")])]})})]});
            var Q2;
            Q2=makeQuery(id+"F17.opFillet","BLEND_EDGE",EDGE,{"blendedFrom":[makeQuery(id+"F16.boolean.opBoolean","COPY",EDGE,{"derivedFrom":makeQuery(id+"F16.opExtrude","SWEPT_EDGE",EDGE,{"disambiguationData":[OSD([sQuery(id+"F15.wireOp",EDGE,"E127"),sQuery(id+"F15.wireOp",EDGE,"E143"),sQuery(id+"F15.wireOp",EDGE,"E144")])]})}),makeQuery(id+"F16.boolean.opBoolean","COPY",FACE,{"derivedFrom":makeQuery(id+"F16.opExtrude","SWEPT_FACE",FACE,{"disambiguationData":[OSD([sQuery(id+"F15.wireOp",EDGE,"E204")])]})})],"blendedInto":[makeQuery(id+"F16.boolean.opBoolean","COPY",FACE,{"derivedFrom":makeQuery(id+"F16.opExtrude","SWEPT_FACE",FACE,{"disambiguationData":[OSD([sQuery(id+"F15.wireOp",EDGE,"E204")])]})})]});
            var Q3;
            Q3=makeQuery(id+"F17.opFillet","BLEND_EDGE",EDGE,{"blendedFrom":[makeQuery(id+"F16.boolean.opBoolean","COPY",EDGE,{"derivedFrom":makeQuery(id+"F16.opExtrude","SWEPT_EDGE",EDGE,{"disambiguationData":[OSD([sQuery(id+"F15.wireOp",EDGE,"E179"),sQuery(id+"F15.wireOp",EDGE,"E201")])]})}),makeQuery(id+"F16.boolean.opBoolean","COPY",FACE,{"derivedFrom":makeQuery(id+"F16.opExtrude","SWEPT_FACE",FACE,{"disambiguationData":[OSD([sQuery(id+"F15.wireOp",EDGE,"E177")])]})})],"blendedInto":[makeQuery(id+"F16.boolean.opBoolean","COPY",FACE,{"derivedFrom":makeQuery(id+"F16.opExtrude","SWEPT_FACE",FACE,{"disambiguationData":[OSD([sQuery(id+"F15.wireOp",EDGE,"E177")])]})})]});
            var Q4;
            Q4=makeQuery(id+"F17.opFillet","BLEND_EDGE",EDGE,{"blendedFrom":[makeQuery(id+"F16.boolean.opBoolean","COPY",EDGE,{"derivedFrom":makeQuery(id+"F16.opExtrude","SWEPT_EDGE",EDGE,{"disambiguationData":[OSD([sQuery(id+"F15.wireOp",EDGE,"E181.MirrorCS"),sQuery(id+"F15.wireOp",EDGE,"E197")])]})}),makeQuery(id+"F16.boolean.opBoolean","COPY",FACE,{"derivedFrom":makeQuery(id+"F16.opExtrude","SWEPT_FACE",FACE,{"disambiguationData":[OSD([sQuery(id+"F15.wireOp",EDGE,"E183.MirrorC")])]})})],"blendedInto":[makeQuery(id+"F16.boolean.opBoolean","COPY",FACE,{"derivedFrom":makeQuery(id+"F16.opExtrude","SWEPT_FACE",FACE,{"disambiguationData":[OSD([sQuery(id+"F15.wireOp",EDGE,"E183.MirrorC")])]})})]});
            var Q5;
            Q5=makeQuery(id+"F16.boolean.opBoolean","COPY",EDGE,{"derivedFrom":makeQuery(id+"F16.opExtrude","SWEPT_EDGE",EDGE,{"disambiguationData":[OSD([sQuery(id+"F15.wireOp",EDGE,"E180"),sQuery(id+"F15.wireOp",EDGE,"E207")])]})});
            var Q6;
            Q6=makeQuery(id+"F16.boolean.opBoolean","COPY",EDGE,{"derivedFrom":makeQuery(id+"F16.opExtrude","SWEPT_EDGE",EDGE,{"disambiguationData":[OSD([sQuery(id+"F15.wireOp",EDGE,"E153"),sQuery(id+"F15.wireOp",EDGE,"E207")])]})});
            var Q7;
            Q7=makeQuery(id+"F16.boolean.opBoolean","COPY",EDGE,{"derivedFrom":makeQuery(id+"F16.opExtrude","SWEPT_EDGE",EDGE,{"disambiguationData":[OSD([sQuery(id+"F15.wireOp",EDGE,"E153"),sQuery(id+"F15.wireOp",EDGE,"E208")])]})});
            var Q8;
            Q8=makeQuery(id+"F16.boolean.opBoolean","COPY",EDGE,{"derivedFrom":makeQuery(id+"F16.opExtrude","SWEPT_EDGE",EDGE,{"disambiguationData":[OSD([sQuery(id+"F15.wireOp",EDGE,"E180"),sQuery(id+"F15.wireOp",EDGE,"E208")])]})});
            var Q9;
            Q9=makeQuery(id+"F17.opFillet","BLEND_EDGE",EDGE,{"blendedFrom":[makeQuery(id+"F16.boolean.opBoolean","COPY",EDGE,{"derivedFrom":makeQuery(id+"F16.opExtrude","SWEPT_EDGE",EDGE,{"disambiguationData":[OSD([sQuery(id+"F15.wireOp",EDGE,"E132"),sQuery(id+"F15.wireOp",EDGE,"E137"),sQuery(id+"F15.wireOp",EDGE,"E138")])]})}),makeQuery(id+"F16.boolean.opBoolean","COPY",FACE,{"derivedFrom":makeQuery(id+"F16.opExtrude","SWEPT_FACE",FACE,{"disambiguationData":[OSD([sQuery(id+"F15.wireOp",EDGE,"E196")])]})})],"blendedInto":[makeQuery(id+"F16.boolean.opBoolean","COPY",FACE,{"derivedFrom":makeQuery(id+"F16.opExtrude","SWEPT_FACE",FACE,{"disambiguationData":[OSD([sQuery(id+"F15.wireOp",EDGE,"E196")])]})})]});
            var Q10;
            Q10=makeQuery(id+"F16.boolean.opBoolean","COPY",EDGE,{"derivedFrom":makeQuery(id+"F16.opExtrude","SWEPT_EDGE",EDGE,{"disambiguationData":[OSD([sQuery(id+"F15.wireOp",EDGE,"E134"),sQuery(id+"F15.wireOp",EDGE,"E211")])]})});
            var Q11;
            Q11=makeQuery(id+"F16.boolean.opBoolean","COPY",EDGE,{"derivedFrom":makeQuery(id+"F16.opExtrude","SWEPT_EDGE",EDGE,{"disambiguationData":[OSD([sQuery(id+"F15.wireOp",EDGE,"E150"),sQuery(id+"F15.wireOp",EDGE,"E214")])]})});
            var Q12;
            Q12=makeQuery(id+"F16.boolean.opBoolean","COPY",EDGE,{"derivedFrom":makeQuery(id+"F16.opExtrude","SWEPT_EDGE",EDGE,{"disambiguationData":[OSD([sQuery(id+"F15.wireOp",EDGE,"E134"),sQuery(id+"F15.wireOp",EDGE,"E213")])]})});
            var Q13;
            {var subQ0=sQuery(id+"F15.wireOp",EDGE,"E213");var subQ1=sQuery(id+"F15.wireOp",EDGE,"E150");Q13=makeQuery(id+"F16.boolean.opBoolean","COPY",EDGE,{"derivedFrom":makeQuery(id+"F16.opExtrude","SWEPT_EDGE",EDGE,{"disambiguationData":[OSD([subQ1,subQ0]),TDD([makeQuery(id+"F15.imprint","INTERSECT",VERTEX,{"disambiguationData":[OD(1.0)],"derivedFrom":[subQ1,subQ0]})])]})});}
            var Q14;
            {var subQ0=sQuery(id+"F15.wireOp",EDGE,"E213");var subQ1=sQuery(id+"F15.wireOp",EDGE,"E150");Q14=makeQuery(id+"F16.boolean.opBoolean","COPY",EDGE,{"derivedFrom":makeQuery(id+"F16.opExtrude","SWEPT_EDGE",EDGE,{"disambiguationData":[OSD([subQ1,subQ0]),TDD([makeQuery(id+"F15.imprint","INTERSECT",VERTEX,{"disambiguationData":[OD(0.0)],"derivedFrom":[subQ1,subQ0]})])]})});}
            var Q15;
            Q15=makeQuery(id+"F16.boolean.opBoolean","COPY",EDGE,{"derivedFrom":makeQuery(id+"F16.opExtrude","SWEPT_EDGE",EDGE,{"disambiguationData":[OSD([sQuery(id+"F15.wireOp",EDGE,"E168"),sQuery(id+"F15.wireOp",EDGE,"E213")])]})});
            var Q16;
            Q16=makeQuery(id+"F16.boolean.opBoolean","COPY",EDGE,{"derivedFrom":makeQuery(id+"F16.opExtrude","SWEPT_EDGE",EDGE,{"disambiguationData":[OSD([sQuery(id+"F15.wireOp",EDGE,"E168"),sQuery(id+"F15.wireOp",EDGE,"E214")])]})});
            var Q17;
            Q17=makeQuery(id+"F16.boolean.opBoolean","COPY",EDGE,{"derivedFrom":makeQuery(id+"F16.opExtrude","SWEPT_EDGE",EDGE,{"disambiguationData":[OSD([sQuery(id+"F15.wireOp",EDGE,"E150"),sQuery(id+"F15.wireOp",EDGE,"E211")])]})});
            var Q18;
            {var subQ0=sQuery(id+"F15.wireOp",EDGE,"E218");var subQ1=sQuery(id+"F15.wireOp",EDGE,"E149");Q18=makeQuery(id+"F16.boolean.opBoolean","COPY",EDGE,{"derivedFrom":makeQuery(id+"F16.opExtrude","SWEPT_EDGE",EDGE,{"disambiguationData":[OSD([subQ1,subQ0]),TDD([makeQuery(id+"F15.imprint","INTERSECT",VERTEX,{"disambiguationData":[OD(0.0)],"derivedFrom":[subQ1,subQ0]})])]})});}
            var Q19;
            Q19=makeQuery(id+"F16.boolean.opBoolean","COPY",EDGE,{"derivedFrom":makeQuery(id+"F16.opExtrude","SWEPT_EDGE",EDGE,{"disambiguationData":[OSD([sQuery(id+"F15.wireOp",EDGE,"E144"),sQuery(id+"F15.wireOp",EDGE,"E218")])]})});
            var Q20;
            {var subQ0=sQuery(id+"F15.wireOp",EDGE,"E220");var subQ1=sQuery(id+"F15.wireOp",EDGE,"E149");Q20=makeQuery(id+"F16.boolean.opBoolean","COPY",EDGE,{"derivedFrom":makeQuery(id+"F16.opExtrude","SWEPT_EDGE",EDGE,{"disambiguationData":[OSD([subQ1,subQ0]),TDD([makeQuery(id+"F15.imprint","INTERSECT",VERTEX,{"disambiguationData":[OD(0.0)],"derivedFrom":[subQ1,subQ0]})])]})});}
            var Q21;
            Q21=makeQuery(id+"F16.boolean.opBoolean","COPY",EDGE,{"derivedFrom":makeQuery(id+"F16.opExtrude","SWEPT_EDGE",EDGE,{"disambiguationData":[OSD([sQuery(id+"F15.wireOp",EDGE,"E144"),sQuery(id+"F15.wireOp",EDGE,"E220")])]})});
            var Q22;
            {var subQ0=sQuery(id+"F15.wireOp",EDGE,"E218");var subQ1=sQuery(id+"F15.wireOp",EDGE,"E149");Q22=makeQuery(id+"F16.boolean.opBoolean","COPY",EDGE,{"derivedFrom":makeQuery(id+"F16.opExtrude","SWEPT_EDGE",EDGE,{"disambiguationData":[OSD([subQ1,subQ0]),TDD([makeQuery(id+"F15.imprint","INTERSECT",VERTEX,{"disambiguationData":[OD(1.0)],"derivedFrom":[subQ1,subQ0]})])]})});}
            var Q23;
            Q23=makeQuery(id+"F16.boolean.opBoolean","COPY",EDGE,{"derivedFrom":makeQuery(id+"F16.opExtrude","SWEPT_EDGE",EDGE,{"disambiguationData":[OSD([sQuery(id+"F15.wireOp",EDGE,"E168"),sQuery(id+"F15.wireOp",EDGE,"E218")])]})});
            var Q24;
            {var subQ0=sQuery(id+"F15.wireOp",EDGE,"E220");var subQ1=sQuery(id+"F15.wireOp",EDGE,"E149");Q24=makeQuery(id+"F16.boolean.opBoolean","COPY",EDGE,{"derivedFrom":makeQuery(id+"F16.opExtrude","SWEPT_EDGE",EDGE,{"disambiguationData":[OSD([subQ1,subQ0]),TDD([makeQuery(id+"F15.imprint","INTERSECT",VERTEX,{"disambiguationData":[OD(1.0)],"derivedFrom":[subQ1,subQ0]})])]})});}
            var Q25;
            Q25=makeQuery(id+"F16.boolean.opBoolean","COPY",EDGE,{"derivedFrom":makeQuery(id+"F16.opExtrude","SWEPT_EDGE",EDGE,{"disambiguationData":[OSD([sQuery(id+"F15.wireOp",EDGE,"E168"),sQuery(id+"F15.wireOp",EDGE,"E220")])]})});
            fillet(context, id + "F18", {"entities" : qUnion([Q0, Q1, Q2, Q3, Q4, Q5, Q6, Q7, Q8, Q9, Q10, Q11, Q12, Q13, Q14, Q15, Q16, Q17, Q18, Q19, Q20, Q21, Q22, Q23, Q24, Q25]), "radius" : 2 * mm, "tangentPropagation" : true, "allowEdgeOverflow" : false});
        }
    });
